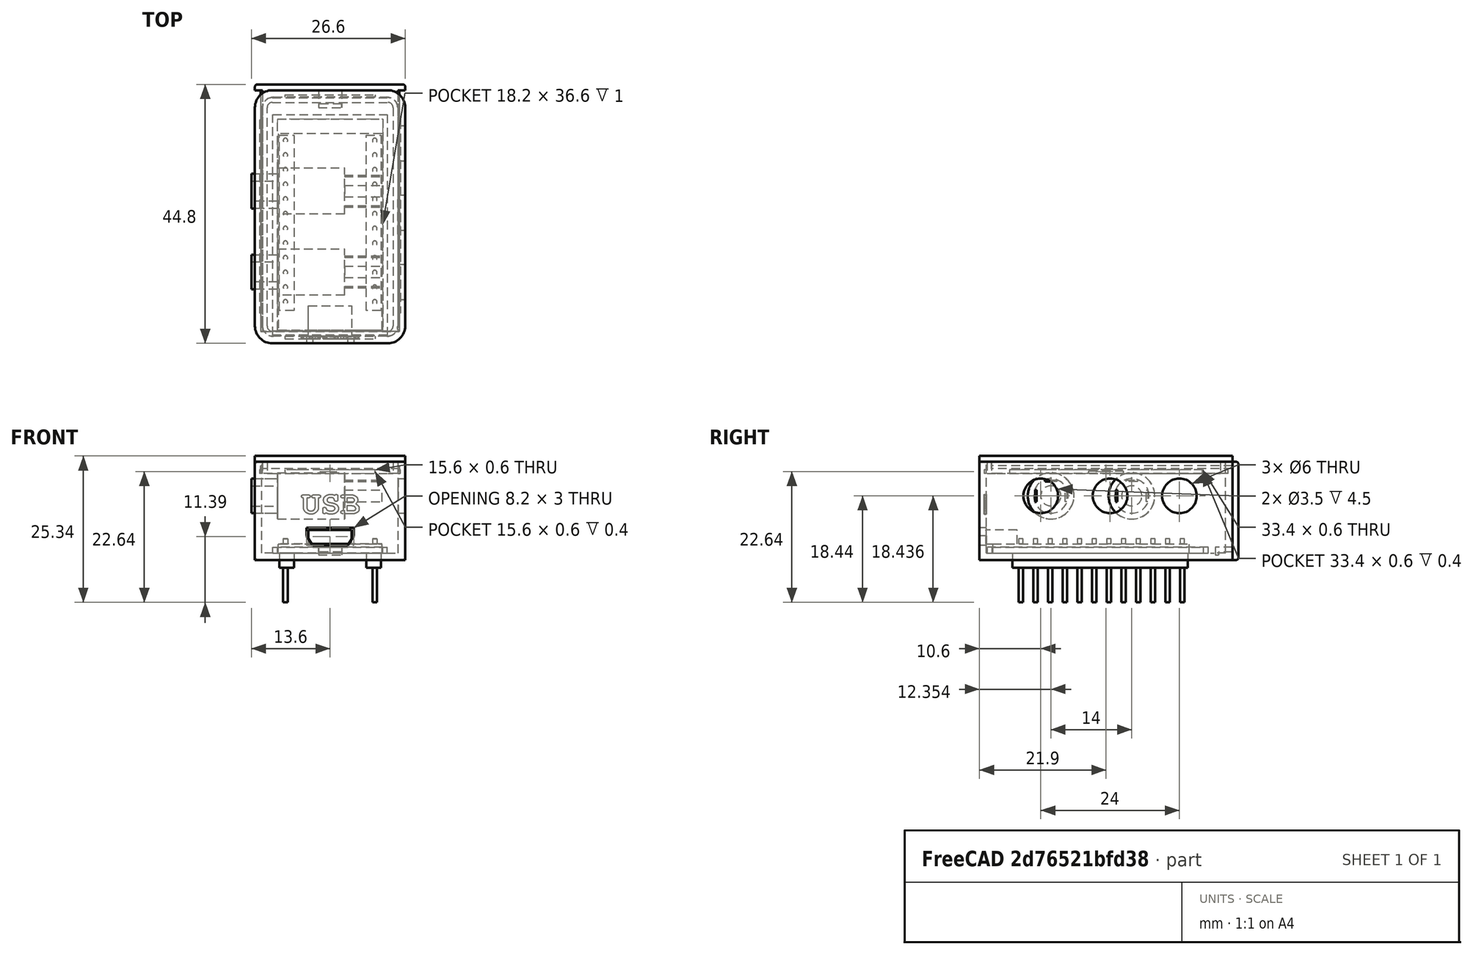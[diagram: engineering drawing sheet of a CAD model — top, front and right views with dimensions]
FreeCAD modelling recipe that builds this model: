
FCSTD DOCUMENT  (FreeCAD 0.18R4 (GitTag))
Label: FABI_mini
License: All rights reserved
LicenseURL: http://en.wikipedia.org/wiki/All_rights_reserved
objects: Sketcher::SketchObject×25, PartDesign::Pad×19, PartDesign::Body×6, PartDesign::Pocket×5, PartDesign::Fillet×4, Mesh::Feature×3, Part::Part2DObjectPython×2, Part::Extrusion×2, Part::Cut×2, PartDesign::Mirrored×1
note: 90 computed .brp shape members not serialized (recipe doc carries the construction recipe); baked Part::Feature solids carry a one-line shape summary decoded from their .brp

FEATURE [Sketcher::SketchObject] Sketch
  MapMode = 5
  Support = -> [XY_Plane]
  sketch-geometry (4):
    g0: LineSegment StartX=-13 StartY=24.5 StartZ=0 EndX=13 EndY=24.5 EndZ=0
    g1: LineSegment StartX=13 StartY=24.5 StartZ=0 EndX=13 EndY=-19.3 EndZ=0
    g2: LineSegment StartX=13 StartY=-19.3 StartZ=0 EndX=-13 EndY=-19.3 EndZ=0
    g3: LineSegment StartX=-13 StartY=-19.3 StartZ=0 EndX=-13 EndY=24.5 EndZ=0
  constraints (12):
    c: Coincident(g0,g1)
    c: Coincident(g1,g2)
    c: Coincident(g2,g3)
    c: Coincident(g3,g0)
    c: Horizontal(g0)
    c: Horizontal(g2)
    c: Vertical(g1)
    c: Vertical(g3)
    c: DistanceX(g0,g0) = 26
    c: DistanceY(g3,g3) = 43.8
    c: DistanceY(g2,g-1) = 19.3
    c: DistanceX(g2,g-1) = 13
FEATURE [PartDesign::Pad] Pad
  Length = 17
  Length2 = 100
  Profile = -> Sketch
  Refine = true
  Type = 0
FEATURE [Sketcher::SketchObject] CopyCopySketch002
  sketch-geometry (34):
    g0: Circle CenterX=32.8 CenterY=1.27 CenterZ=0 NormalX=0 NormalY=0 NormalZ=1 AngleXU=0 Radius=0.4
    g1: Circle CenterX=30.26 CenterY=1.27 CenterZ=0 NormalX=0 NormalY=0 NormalZ=1 AngleXU=0 Radius=0.4
    g2: Circle CenterX=27.72 CenterY=1.27 CenterZ=0 NormalX=0 NormalY=0 NormalZ=1 AngleXU=0 Radius=0.4
    g3: Circle CenterX=25.18 CenterY=1.27 CenterZ=0 NormalX=0 NormalY=0 NormalZ=1 AngleXU=0 Radius=0.4
    g4: Circle CenterX=22.64 CenterY=1.27 CenterZ=0 NormalX=0 NormalY=0 NormalZ=1 AngleXU=0 Radius=0.4
    g5: Circle CenterX=20.1 CenterY=1.27 CenterZ=0 NormalX=0 NormalY=0 NormalZ=1 AngleXU=0 Radius=0.4
    g6: Circle CenterX=17.56 CenterY=1.27 CenterZ=0 NormalX=0 NormalY=0 NormalZ=1 AngleXU=0 Radius=0.4
    g7: Circle CenterX=15.02 CenterY=1.27 CenterZ=0 NormalX=0 NormalY=0 NormalZ=1 AngleXU=0 Radius=0.4
    g8: Circle CenterX=12.48 CenterY=1.27 CenterZ=0 NormalX=0 NormalY=0 NormalZ=1 AngleXU=0 Radius=0.4
    g9: Circle CenterX=9.94 CenterY=1.27 CenterZ=0 NormalX=0 NormalY=0 NormalZ=1 AngleXU=0 Radius=0.4
    g10: Circle CenterX=7.4 CenterY=1.27 CenterZ=0 NormalX=0 NormalY=0 NormalZ=1 AngleXU=0 Radius=0.4
    g11: Circle CenterX=4.86 CenterY=1.27 CenterZ=0 NormalX=0 NormalY=0 NormalZ=1 AngleXU=0 Radius=0.4
    g12: LineSegment [constr] StartX=33.2 StartY=1.27 StartZ=0 EndX=3.66 EndY=1.27 EndZ=0
    g13: LineSegment [constr] StartX=34 StartY=0 StartZ=0 EndX=3.66 EndY=0 EndZ=0
    g14: LineSegment [constr] StartX=3.66 StartY=0 StartZ=0 EndX=3.66 EndY=2.54 EndZ=0
    g15: LineSegment [constr] StartX=3.66 StartY=2.54 StartZ=0 EndX=34 EndY=2.54 EndZ=0
    g16: LineSegment [constr] StartX=34 StartY=2.54 StartZ=0 EndX=34 EndY=0 EndZ=0
    g17: Circle CenterX=32.8 CenterY=16.73 CenterZ=0 NormalX=0 NormalY=0 NormalZ=1 AngleXU=0 Radius=0.4
    g18: Circle CenterX=30.26 CenterY=16.73 CenterZ=0 NormalX=0 NormalY=0 NormalZ=1 AngleXU=0 Radius=0.4
    g19: Circle CenterX=27.72 CenterY=16.73 CenterZ=0 NormalX=0 NormalY=0 NormalZ=1 AngleXU=0 Radius=0.4
    g20: Circle CenterX=25.18 CenterY=16.73 CenterZ=0 NormalX=0 NormalY=0 NormalZ=1 AngleXU=0 Radius=0.4
    g21: Circle CenterX=22.64 CenterY=16.73 CenterZ=0 NormalX=0 NormalY=0 NormalZ=1 AngleXU=0 Radius=0.4
    g22: Circle CenterX=20.1 CenterY=16.73 CenterZ=0 NormalX=0 NormalY=0 NormalZ=1 AngleXU=0 Radius=0.4
    g23: Circle CenterX=17.56 CenterY=16.73 CenterZ=0 NormalX=0 NormalY=0 NormalZ=1 AngleXU=0 Radius=0.4
    g24: Circle CenterX=15.02 CenterY=16.73 CenterZ=0 NormalX=0 NormalY=0 NormalZ=1 AngleXU=0 Radius=0.4
    g25: Circle CenterX=12.48 CenterY=16.73 CenterZ=0 NormalX=0 NormalY=0 NormalZ=1 AngleXU=0 Radius=0.4
    g26: Circle CenterX=9.94 CenterY=16.73 CenterZ=0 NormalX=0 NormalY=0 NormalZ=1 AngleXU=0 Radius=0.4
    g27: Circle CenterX=7.4 CenterY=16.73 CenterZ=0 NormalX=0 NormalY=0 NormalZ=1 AngleXU=0 Radius=0.4
    g28: Circle CenterX=4.86 CenterY=16.73 CenterZ=0 NormalX=0 NormalY=0 NormalZ=1 AngleXU=0 Radius=0.4
    g29: LineSegment [constr] StartX=33.2 StartY=16.73 StartZ=0 EndX=3.66 EndY=16.73 EndZ=0
    g30: LineSegment [constr] StartX=34 StartY=15.46 StartZ=0 EndX=3.66 EndY=15.46 EndZ=0
    g31: LineSegment [constr] StartX=3.66 StartY=15.46 StartZ=0 EndX=3.66 EndY=18 EndZ=0
    g32: LineSegment [constr] StartX=3.66 StartY=18 StartZ=0 EndX=34 EndY=18 EndZ=0
    g33: LineSegment [constr] StartX=34 StartY=18 StartZ=0 EndX=34 EndY=15.46 EndZ=0
  constraints (104):
    c: Radius(g0) = 0.4
    c: Equal(g0,g1) = 0.4
    c: Equal(g0,g2) = 0.4
    c: Equal(g2,g3) = 0.4
    c: Equal(g0,g4) = 0.4
    c: Equal(g4,g5) = 0.4
    c: Equal(g4,g6) = 0.4
    c: Equal(g6,g7) = 0.4
    c: Equal(g8,g9) = 0.4
    c: Equal(g8,g10) = 0.4
    c: Equal(g10,g11) = 0.4
    c: Horizontal(g12)
    c: PointOnObject(g11,g12)
    c: PointOnObject(g10,g12)
    c: PointOnObject(g9,g12)
    c: PointOnObject(g8,g12)
    c: PointOnObject(g7,g12)
    c: PointOnObject(g6,g12)
    c: PointOnObject(g5,g12)
    c: PointOnObject(g4,g12)
    c: PointOnObject(g3,g12)
    c: PointOnObject(g2,g12)
    c: PointOnObject(g1,g12)
    c: PointOnObject(g0,g12)
    c: DistanceX(g1,g0) = 2.54
    c: DistanceX(g2,g1) = 2.54
    c: DistanceX(g3,g2) = 2.54
    c: DistanceX(g4,g3) = 2.54
    c: DistanceX(g5,g4) = 2.54
    c: DistanceX(g6,g5) = 2.54
    c: DistanceX(g7,g6) = 2.54
    c: DistanceX(g8,g7) = 2.54
    c: DistanceX(g9,g8) = 2.54
    c: DistanceX(g10,g9) = 2.54
    c: DistanceX(g11,g10) = 2.54
    c: Coincident(g13,g14)
    c: Coincident(g14,g15)
    c: Coincident(g15,g16)
    c: Coincident(g16,g13)
    c: Horizontal(g13)
    c: Horizontal(g15)
    c: Vertical(g14)
    c: Vertical(g16)
    c: DistanceY(g14,g14) = 2.54
    c: DistanceY(g13,g0) = 1.27
    c: DistanceX(g12,g15) = 0.8
    c: PointOnObject(g12,g0)
    c: Equal(g7,g8)
    c: DistanceX(g14,g11) = 1.2
    c: Equal(g0,g17) = 0.4
    c: Equal(g17,g18) = 0.4
    c: Equal(g17,g19) = 0.4
    c: Equal(g19,g20) = 0.4
    c: Equal(g17,g21) = 0.4
    c: Equal(g21,g22) = 0.4
    c: Equal(g21,g23) = 0.4
    c: Equal(g23,g24) = 0.4
    c: Equal(g25,g26) = 0.4
    c: Equal(g25,g27) = 0.4
    c: Equal(g27,g28) = 0.4
    c: Horizontal(g29)
    c: PointOnObject(g28,g29)
    c: PointOnObject(g27,g29)
    c: PointOnObject(g26,g29)
    c: PointOnObject(g25,g29)
    c: PointOnObject(g24,g29)
    c: PointOnObject(g23,g29)
    c: PointOnObject(g22,g29)
    c: PointOnObject(g21,g29)
    c: PointOnObject(g20,g29)
    c: PointOnObject(g19,g29)
    c: PointOnObject(g18,g29)
    c: PointOnObject(g17,g29)
    c: DistanceX(g18,g17) = 2.54
    c: DistanceX(g19,g18) = 2.54
    c: DistanceX(g20,g19) = 2.54
    c: DistanceX(g21,g20) = 2.54
    c: DistanceX(g22,g21) = 2.54
    c: DistanceX(g23,g22) = 2.54
    c: DistanceX(g24,g23) = 2.54
    c: DistanceX(g25,g24) = 2.54
    c: DistanceX(g26,g25) = 2.54
    c: DistanceX(g27,g26) = 2.54
    c: DistanceX(g28,g27) = 2.54
    c: Coincident(g30,g31)
    c: Coincident(g31,g32)
    c: Coincident(g32,g33)
    c: Coincident(g33,g30)
    c: Horizontal(g30)
    c: Horizontal(g32)
    c: Vertical(g31)
    c: Vertical(g33)
    c: Equal(g14,g31) = 2.54
    c: DistanceY(g30,g17) = 1.27
    c: DistanceX(g29,g32) = 0.8
    c: PointOnObject(g29,g17)
    c: Equal(g24,g25)
    c: DistanceX(g31,g28) = 1.2
    c: PointOnObject(g12,g14)
    c: PointOnObject(g29,g31)
    c: DistanceY(g-1,g31) = 18
    c: DistanceX(g30,g14) = 0
    c: DistanceY(g13,g-1) = 0
    c: DistanceX(g-1,g13) = 3.66
FEATURE [Sketcher::SketchObject] Sketch001
  MapMode = 5
  Support = -> [XY_Plane001]
  sketch-geometry (4):
    g0: LineSegment StartX=0 StartY=0 StartZ=0 EndX=34 EndY=0 EndZ=0
    g1: LineSegment StartX=34 StartY=0 StartZ=0 EndX=34 EndY=18 EndZ=0
    g2: LineSegment StartX=34 StartY=18 StartZ=0 EndX=0 EndY=18 EndZ=0
    g3: LineSegment StartX=0 StartY=18 StartZ=0 EndX=0 EndY=0 EndZ=0
  constraints (11):
    c: Coincident(g2,g3)
    c: Coincident(g3,g0)
    c: Horizontal(g0)
    c: Horizontal(g2)
    c: Vertical(g1)
    c: Vertical(g3)
    c: Coincident(g0,g-1)
    c: DistanceY(g3,g3) = 18
    c: DistanceX(g2,g2) = 34
    c: Coincident(g1,g0)
    c: Coincident(g2,g1)
FEATURE [PartDesign::Pad] Pad001
  Length = 1.6
  Length2 = 100
  Profile = -> Sketch001
  Refine = true
  Type = 0
FEATURE [Sketcher::SketchObject] Sketch002
  MapMode = 5
  Support = -> [XY_Plane001]
  sketch-geometry (8):
    g0: LineSegment StartX=3.4 StartY=17.8 StartZ=0 EndX=33.74 EndY=17.8 EndZ=0
    g1: LineSegment StartX=33.74 StartY=17.8 StartZ=0 EndX=33.74 EndY=15.26 EndZ=0
    g2: LineSegment StartX=33.74 StartY=15.26 StartZ=0 EndX=3.4 EndY=15.26 EndZ=0
    g3: LineSegment StartX=3.4 StartY=15.26 StartZ=0 EndX=3.4 EndY=17.8 EndZ=0
    g4: LineSegment StartX=3.4 StartY=2.74 StartZ=0 EndX=33.74 EndY=2.74 EndZ=0
    g5: LineSegment StartX=33.74 StartY=2.74 StartZ=0 EndX=33.74 EndY=0.2 EndZ=0
    g6: LineSegment StartX=33.74 StartY=0.2 StartZ=0 EndX=3.4 EndY=0.2 EndZ=0
    g7: LineSegment StartX=3.4 StartY=0.2 StartZ=0 EndX=3.4 EndY=2.74 EndZ=0
  constraints (24):
    c: Coincident(g0,g1)
    c: Coincident(g1,g2)
    c: Coincident(g2,g3)
    c: Coincident(g3,g0)
    c: Horizontal(g0)
    c: Horizontal(g2)
    c: Vertical(g1)
    c: Vertical(g3)
    c: DistanceX(g0,g0) = 30.34
    c: DistanceY(g3,g3) = 2.54
    c: DistanceX(g-1,g2) = 3.4
    c: Coincident(g4,g5)
    c: Coincident(g5,g6)
    c: Coincident(g6,g7)
    c: Coincident(g7,g4)
    c: Horizontal(g4)
    c: Horizontal(g6)
    c: Vertical(g5)
    c: Vertical(g7)
    c: Equal(g0,g4) = 30.34
    c: Equal(g3,g7) = 2.54
    c: DistanceY(g-1,g6) = 0.2
    c: DistanceX(g2,g4) = 0
    c: DistanceY(g6,g0) = 17.6
FEATURE [PartDesign::Pad] Pad002  label="PinHeaderBody"
  BaseFeature = -> Pad001
  Length = 2.54
  Length2 = 100
  Profile = -> Sketch002
  Refine = true
  Reversed = true
  Type = 0
FEATURE [PartDesign::Pad] Pad003  label="PinHeaderPins"
  BaseFeature = -> Pad002
  Length = 2.5
  Length2 = 8.54
  Profile = -> CopyCopySketch002
  Refine = true
  Reversed = true
  Type = 4
FEATURE [Sketcher::SketchObject] Sketch003  label="microUsb"
  MapMode = 5
  Placement = pos=(0,0,1.6) rot=(0,0,1;0rad)
  Support = -> [Pad003]
  sketch-geometry (4):
    g0: LineSegment StartX=-1.2 StartY=12.75 StartZ=0 EndX=4.2 EndY=12.75 EndZ=0
    g1: LineSegment StartX=4.2 StartY=12.75 StartZ=0 EndX=4.2 EndY=5.25 EndZ=0
    g2: LineSegment StartX=4.2 StartY=5.25 StartZ=0 EndX=-1.2 EndY=5.25 EndZ=0
    g3: LineSegment StartX=-1.2 StartY=5.25 StartZ=0 EndX=-1.2 EndY=12.75 EndZ=0
  constraints (12):
    c: Coincident(g0,g1)
    c: Coincident(g1,g2)
    c: Coincident(g2,g3)
    c: Coincident(g3,g0)
    c: Horizontal(g0)
    c: Horizontal(g2)
    c: Vertical(g1)
    c: Vertical(g3)
    c: DistanceY(g3,g3) = 7.5
    c: DistanceX(g0,g0) = 5.4
    c: DistanceX(g2,g-1) = 1.2
    c: DistanceY(g-1,g2) = 5.25
FEATURE [PartDesign::Pad] Pad004  label="MicroUSB"
  BaseFeature = -> Pad003
  Length = 2.4
  Length2 = 100
  Profile = -> Sketch003
  Refine = true
  Type = 0
FEATURE [PartDesign::Body] Body001  label="ProMicro001"
  Group = -> [Sketch001,Pad001,Sketch002,Pad002,Pad003,Sketch003,Pad004]
  Origin = -> Origin001
  Placement = pos=(9,-17,1.2) rot=(0,0,1;1.5708rad)
  Tip = -> Pad004
FEATURE [Sketcher::SketchObject] Sketch004
  ExternalGeometry = -> [Sketch]
  MapMode = 5
  Placement = pos=(0,0,1.2) rot=(0,0,1;0rad)
  sketch-geometry (4):
    g0: LineSegment StartX=-11.8 StartY=23.3 StartZ=0 EndX=11.8 EndY=23.3 EndZ=0
    g1: LineSegment StartX=11.8 StartY=23.3 StartZ=0 EndX=11.8 EndY=-18.1 EndZ=0
    g2: LineSegment StartX=11.8 StartY=-18.1 StartZ=0 EndX=-11.8 EndY=-18.1 EndZ=0
    g3: LineSegment StartX=-11.8 StartY=-18.1 StartZ=0 EndX=-11.8 EndY=23.3 EndZ=0
  constraints (12):
    c: Coincident(g0,g1)
    c: Coincident(g1,g2)
    c: Coincident(g2,g3)
    c: Horizontal(g0)
    c: Horizontal(g2)
    c: Vertical(g1)
    c: Vertical(g3)
    c: Coincident(g0,g3)
    c: DistanceY(g-3,g2) = 1.2
    c: DistanceY(g-4,g0) = -1.2
    c: DistanceX(g1,g-4) = 1.2
    c: DistanceX(g-3,g2) = 1.2
FEATURE [PartDesign::Pocket] Pocket
  BaseFeature = -> Pad
  Length = 31
  Length2 = 100
  Profile = -> Sketch004
  Refine = true
  Reversed = true
  Type = 1
FEATURE [Sketcher::SketchObject] Sketch006  label="ProMicro"
  MapMode = 5
  Placement = pos=(0,-18.1,0) rot=(0,0.707107,0.707107;3.14159rad)
  Support = -> [Pocket]
  sketch-geometry (6):
    g0: LineSegment StartX=-4.1 StartY=5.55 StartZ=0 EndX=4.1 EndY=5.55 EndZ=0
    g1: LineSegment StartX=4.1 StartY=5.55 StartZ=0 EndX=4.1 EndY=4.15 EndZ=0
    g2: LineSegment StartX=-4.1 StartY=4.15 StartZ=0 EndX=-4.1 EndY=5.55 EndZ=0
    g3: LineSegment StartX=-3 StartY=2.55 StartZ=0 EndX=3 EndY=2.55 EndZ=0
    g4: LineSegment StartX=3 StartY=2.55 StartZ=0 EndX=4.1 EndY=4.15 EndZ=0
    g5: LineSegment StartX=-4.1 StartY=4.15 StartZ=0 EndX=-3 EndY=2.55 EndZ=0
  constraints (18):
    c: Coincident(g0,g1)
    c: Coincident(g2,g0)
    c: Horizontal(g0)
    c: Vertical(g1)
    c: Vertical(g2)
    c: DistanceX(g0,g0) = 8.2
    c: Horizontal(g3)
    c: DistanceY(g3,g0) = 3
    c: DistanceY(g1,g1) = 1.4
    c: Coincident(g4,g3)
    c: Coincident(g4,g1)
    c: Equal(g2,g1)
    c: Coincident(g5,g2)
    c: Coincident(g5,g3)
    c: Equal(g5,g4)
    c: DistanceX(g3,g3) = 6
    c: DistanceX(g3,g-1) = 3
    c: DistanceY(g-1,g3) = 2.55
FEATURE [PartDesign::Pocket] Pocket001  label="ProMicroCut"
  BaseFeature = -> Pocket
  Length = 5
  Length2 = 100
  Profile = -> Sketch006
  Refine = true
  Type = 2
FEATURE [Sketcher::SketchObject] Sketch007
  MapMode = 5
  Placement = pos=(0,0,0) rot=(0.57735,0.57735,0.57735;2.0944rad)
  Support = -> [YZ_Plane002]
  sketch-geometry (1):
    g0: Circle CenterX=-5.05387 CenterY=6.09633 CenterZ=0 NormalX=0 NormalY=0 NormalZ=1 AngleXU=0 Radius=4
  constraints (1):
    c: Radius(g0) = 4
FEATURE [PartDesign::Pad] Pad005
  Length = 11.6
  Length2 = 100
  Placement = pos=(0,0,0) rot=(0.57735,0.57735,0.57735;2.0944rad)
  Profile = -> Sketch007
  Refine = true
  Type = 0
FEATURE [Sketcher::SketchObject] Sketch008
  ExternalGeometry = -> [Pad005]
  MapMode = 5
  Placement = pos=(11.6,-2.6e-15,2.6e-15) rot=(0.57735,0.57735,0.57735;2.0944rad)
  Support = -> [Pad005]
  sketch-geometry (2):
    g0: Circle CenterX=-5.05387 CenterY=6.09633 CenterZ=0 NormalX=0 NormalY=0 NormalZ=1 AngleXU=0 Radius=3
    g1: Circle CenterX=-5.05387 CenterY=6.09633 CenterZ=0 NormalX=0 NormalY=0 NormalZ=1 AngleXU=0 Radius=1.75
  constraints (4):
    c: Radius(g0) = 3
    c: Coincident(g0,g-3)
    c: Coincident(g1,g0)
    c: Radius(g1) = 1.75
FEATURE [PartDesign::Pad] Pad006
  BaseFeature = -> Pad005
  Length = 4.5
  Length2 = 100
  Placement = pos=(0,0,0) rot=(0.57735,0.57735,0.57735;2.0944rad)
  Profile = -> Sketch008
  Refine = true
  Type = 0
FEATURE [Sketcher::SketchObject] Sketch009
  ExternalGeometry = -> [Pad006]
  MapMode = 5
  Placement = pos=(0,0,0) rot=(0.57735,0.57735,-0.57735;4.18879rad)
  Support = -> [Pad006]
  sketch-geometry (12):
    g0: LineSegment StartX=-6.05387 StartY=-8.59633 StartZ=0 EndX=-4.05387 EndY=-8.59633 EndZ=0
    g1: LineSegment StartX=-4.05387 StartY=-8.59633 StartZ=0 EndX=-4.05387 EndY=-8.84633 EndZ=0
    g2: LineSegment StartX=-4.05387 StartY=-8.84633 StartZ=0 EndX=-6.05387 EndY=-8.84633 EndZ=0
    g3: LineSegment StartX=-6.05387 StartY=-8.84633 StartZ=0 EndX=-6.05387 EndY=-8.59633 EndZ=0
    g4: LineSegment StartX=-7.80387 StartY=-5.09633 StartZ=0 EndX=-7.55387 EndY=-5.09633 EndZ=0
    g5: LineSegment StartX=-7.55387 StartY=-5.09633 StartZ=0 EndX=-7.55387 EndY=-7.09633 EndZ=0
    g6: LineSegment StartX=-7.55387 StartY=-7.09633 StartZ=0 EndX=-7.80387 EndY=-7.09633 EndZ=0
    g7: LineSegment StartX=-7.80387 StartY=-7.09633 StartZ=0 EndX=-7.80387 EndY=-5.09633 EndZ=0
    g8: LineSegment StartX=-2.55387 StartY=-5.09633 StartZ=0 EndX=-2.30387 EndY=-5.09633 EndZ=0
    g9: LineSegment StartX=-2.30387 StartY=-5.09633 StartZ=0 EndX=-2.30387 EndY=-7.09633 EndZ=0
    g10: LineSegment StartX=-2.30387 StartY=-7.09633 StartZ=0 EndX=-2.55387 EndY=-7.09633 EndZ=0
    g11: LineSegment StartX=-2.55387 StartY=-7.09633 StartZ=0 EndX=-2.55387 EndY=-5.09633 EndZ=0
  constraints (36):
    c: Coincident(g0,g1)
    c: Coincident(g1,g2)
    c: Coincident(g2,g3)
    c: Coincident(g3,g0)
    c: Horizontal(g0)
    c: Horizontal(g2)
    c: Vertical(g1)
    c: Vertical(g3)
    c: DistanceY(g1,g1) = 0.25
    c: DistanceX(g0,g0) = 2
    c: Coincident(g4,g5)
    c: Coincident(g5,g6)
    c: Coincident(g6,g7)
    c: Coincident(g7,g4)
    c: Horizontal(g4)
    c: Horizontal(g6)
    c: Vertical(g5)
    c: Vertical(g7)
    c: Coincident(g8,g9)
    c: Coincident(g9,g10)
    c: Coincident(g10,g11)
    c: Coincident(g11,g8)
    c: Horizontal(g8)
    c: Horizontal(g10)
    c: Vertical(g9)
    c: Vertical(g11)
    c: DistanceY(g7,g7) = 2
    c: DistanceY(g11,g11) = 2
    c: DistanceX(g4,g4) = 0.25
    c: DistanceX(g8,g8) = 0.25
    c: DistanceX(g5,g-3) = 2.5
    c: DistanceX(g-3,g8) = 2.5
    c: DistanceY(g5,g-3) = 1
    c: DistanceY(g10,g-3) = 1
    c: DistanceY(g0,g-3) = 2.5
    c: DistanceX(g0,g-3) = 1
FEATURE [PartDesign::Pad] Pad007
  BaseFeature = -> Pad006
  Length = 6.5
  Length2 = 100
  Placement = pos=(0,0,0) rot=(0.57735,0.57735,0.57735;2.0944rad)
  Profile = -> Sketch009
  Refine = true
  Type = 0
FEATURE [PartDesign::Body] Body002  label="JackPlug"
  Group = -> [Sketch007,Pad005,Sketch008,Pad006,Sketch009,Pad007]
  Origin = -> Origin002
  Placement = pos=(2.5,-12,5) rot=(0,0,1;3.14159rad)
  Tip = -> Pad007
FEATURE [Sketcher::SketchObject] Sketch010
  MapMode = 5
  Placement = pos=(0,0,0) rot=(0.57735,0.57735,0.57735;2.0944rad)
  Support = -> [YZ_Plane003]
  sketch-geometry (1):
    g0: Circle CenterX=-5.05387 CenterY=6.09633 CenterZ=0 NormalX=0 NormalY=0 NormalZ=1 AngleXU=0 Radius=4
  constraints (1):
    c: Radius(g0) = 4
FEATURE [PartDesign::Pad] Pad009
  Length = 11.6
  Length2 = 100
  Placement = pos=(0,0,0) rot=(0.57735,0.57735,0.57735;2.0944rad)
  Profile = -> Sketch010
  Refine = true
  Type = 0
FEATURE [Sketcher::SketchObject] Sketch012
  ExternalGeometry = -> [Pad009]
  MapMode = 5
  Placement = pos=(11.6,-2.6e-15,2.6e-15) rot=(0.57735,0.57735,0.57735;2.0944rad)
  Support = -> [Pad009]
  sketch-geometry (2):
    g0: Circle CenterX=-5.05387 CenterY=6.09633 CenterZ=0 NormalX=0 NormalY=0 NormalZ=1 AngleXU=0 Radius=3
    g1: Circle CenterX=-5.05387 CenterY=6.09633 CenterZ=0 NormalX=0 NormalY=0 NormalZ=1 AngleXU=0 Radius=1.75
  constraints (4):
    c: Radius(g0) = 3
    c: Coincident(g0,g-3)
    c: Coincident(g1,g0)
    c: Radius(g1) = 1.75
FEATURE [PartDesign::Pad] Pad008
  BaseFeature = -> Pad009
  Length = 4.5
  Length2 = 100
  Placement = pos=(0,0,0) rot=(0.57735,0.57735,0.57735;2.0944rad)
  Profile = -> Sketch012
  Refine = true
  Type = 0
FEATURE [Sketcher::SketchObject] Sketch011
  ExternalGeometry = -> [Pad008]
  MapMode = 5
  Placement = pos=(0,0,0) rot=(0.57735,0.57735,-0.57735;4.18879rad)
  Support = -> [Pad008]
  sketch-geometry (12):
    g0: LineSegment StartX=-6.05387 StartY=-8.59633 StartZ=0 EndX=-4.05387 EndY=-8.59633 EndZ=0
    g1: LineSegment StartX=-4.05387 StartY=-8.59633 StartZ=0 EndX=-4.05387 EndY=-8.84633 EndZ=0
    g2: LineSegment StartX=-4.05387 StartY=-8.84633 StartZ=0 EndX=-6.05387 EndY=-8.84633 EndZ=0
    g3: LineSegment StartX=-6.05387 StartY=-8.84633 StartZ=0 EndX=-6.05387 EndY=-8.59633 EndZ=0
    g4: LineSegment StartX=-7.80387 StartY=-5.09633 StartZ=0 EndX=-7.55387 EndY=-5.09633 EndZ=0
    g5: LineSegment StartX=-7.55387 StartY=-5.09633 StartZ=0 EndX=-7.55387 EndY=-7.09633 EndZ=0
    g6: LineSegment StartX=-7.55387 StartY=-7.09633 StartZ=0 EndX=-7.80387 EndY=-7.09633 EndZ=0
    g7: LineSegment StartX=-7.80387 StartY=-7.09633 StartZ=0 EndX=-7.80387 EndY=-5.09633 EndZ=0
    g8: LineSegment StartX=-2.55387 StartY=-5.09633 StartZ=0 EndX=-2.30387 EndY=-5.09633 EndZ=0
    g9: LineSegment StartX=-2.30387 StartY=-5.09633 StartZ=0 EndX=-2.30387 EndY=-7.09633 EndZ=0
    g10: LineSegment StartX=-2.30387 StartY=-7.09633 StartZ=0 EndX=-2.55387 EndY=-7.09633 EndZ=0
    g11: LineSegment StartX=-2.55387 StartY=-7.09633 StartZ=0 EndX=-2.55387 EndY=-5.09633 EndZ=0
  constraints (36):
    c: Coincident(g0,g1)
    c: Coincident(g1,g2)
    c: Coincident(g2,g3)
    c: Coincident(g3,g0)
    c: Horizontal(g0)
    c: Horizontal(g2)
    c: Vertical(g1)
    c: Vertical(g3)
    c: DistanceY(g1,g1) = 0.25
    c: DistanceX(g0,g0) = 2
    c: Coincident(g4,g5)
    c: Coincident(g5,g6)
    c: Coincident(g6,g7)
    c: Coincident(g7,g4)
    c: Horizontal(g4)
    c: Horizontal(g6)
    c: Vertical(g5)
    c: Vertical(g7)
    c: Coincident(g8,g9)
    c: Coincident(g9,g10)
    c: Coincident(g10,g11)
    c: Coincident(g11,g8)
    c: Horizontal(g8)
    c: Horizontal(g10)
    c: Vertical(g9)
    c: Vertical(g11)
    c: DistanceY(g7,g7) = 2
    c: DistanceY(g11,g11) = 2
    c: DistanceX(g4,g4) = 0.25
    c: DistanceX(g8,g8) = 0.25
    c: DistanceX(g5,g-3) = 2.5
    c: DistanceX(g-3,g8) = 2.5
    c: DistanceY(g5,g-3) = 1
    c: DistanceY(g10,g-3) = 1
    c: DistanceY(g0,g-3) = 2.5
    c: DistanceX(g0,g-3) = 1
FEATURE [PartDesign::Pad] Pad010
  BaseFeature = -> Pad008
  Length = 6.5
  Length2 = 100
  Placement = pos=(0,0,0) rot=(0.57735,0.57735,0.57735;2.0944rad)
  Profile = -> Sketch011
  Refine = true
  Type = 0
FEATURE [PartDesign::Body] Body003  label="JackPlug001"
  Group = -> [Sketch010,Pad009,Sketch012,Pad008,Sketch011,Pad010]
  Origin = -> Origin003
  Placement = pos=(2.5,2,5) rot=(0,0,1;3.14159rad)
  Tip = -> Pad010
FEATURE [Sketcher::SketchObject] Sketch013
  MapMode = 5
  Placement = pos=(13,0,0) rot=(0.57735,0.57735,0.57735;2.0944rad)
  Support = -> [Pocket001]
  sketch-geometry (3):
    g0: Circle CenterX=-8.7 CenterY=11.1 CenterZ=0 NormalX=0 NormalY=0 NormalZ=1 AngleXU=0 Radius=3
    g1: Circle CenterX=3.3 CenterY=11.1 CenterZ=0 NormalX=0 NormalY=0 NormalZ=1 AngleXU=0 Radius=3
    g2: Circle CenterX=15.3 CenterY=11.1 CenterZ=0 NormalX=0 NormalY=0 NormalZ=1 AngleXU=0 Radius=3
  constraints (9):
    c: Radius(g0) = 3
    c: DistanceY(g-1,g0) = 11.1
    c: DistanceX(g0,g-1) = 8.7
    c: Equal(g0,g1) = 3.2
    c: Horizontal(g0,g1)
    c: DistanceX(g0,g1) = 12
    c: Horizontal(g2,g1)
    c: DistanceX(g1,g2) = 12
    c: Equal(g2,g1)
FEATURE [PartDesign::Pocket] Pocket002
  BaseFeature = -> Pocket001
  Length = 5
  Length2 = 100
  Offset = 5
  Profile = -> Sketch013
  Refine = true
  Type = 0
FEATURE [Sketcher::SketchObject] Sketch015
  MapMode = 5
  Placement = pos=(0,25.5,0) rot=(1,0,0;1.5708rad)
  sketch-geometry (4):
    g0: LineSegment StartX=-13 StartY=17 StartZ=0 EndX=13 EndY=17 EndZ=0
    g1: LineSegment StartX=13 StartY=17 StartZ=0 EndX=13 EndY=0 EndZ=0
    g2: LineSegment StartX=13 StartY=0 StartZ=0 EndX=-13 EndY=0 EndZ=0
    g3: LineSegment StartX=-13 StartY=0 StartZ=0 EndX=-13 EndY=17 EndZ=0
  constraints (11):
    c: Coincident(g0,g1)
    c: Coincident(g1,g2)
    c: Coincident(g2,g3)
    c: Coincident(g3,g0)
    c: Horizontal(g0)
    c: Horizontal(g2)
    c: Vertical(g1)
    c: Vertical(g3)
    c: Symmetric(g2,g1,g-1)
    c: DistanceX(g2,g1) = 26
    c: DistanceY(g3,g3) = 17
FEATURE [PartDesign::Pad] Pad011
  Length = 1
  Length2 = 100
  Placement = pos=(0,25.5,0) rot=(1,0,0;1.5708rad)
  Profile = -> Sketch015
  Refine = true
  Reversed = true
  Type = 0
FEATURE [Sketcher::SketchObject] Sketch016
  ExternalGeometry = -> [Pad011]
  MapMode = 5
  Placement = pos=(0,25.5,0) rot=(1,0,0;1.5708rad)
  Support = -> [Pad011]
  sketch-geometry (11):
    g0: LineSegment [constr] StartX=-12 StartY=16.3 StartZ=0 EndX=12 EndY=16.3 EndZ=0
    g1: LineSegment StartX=12 StartY=16.3 StartZ=0 EndX=12 EndY=15.8 EndZ=0
    g2: LineSegment StartX=12 StartY=15.8 StartZ=0 EndX=-12 EndY=15.8 EndZ=0
    g3: LineSegment StartX=-12 StartY=15.8 StartZ=0 EndX=-12 EndY=16.3 EndZ=0
    g4: LineSegment [constr] StartX=-12 StartY=15.8 StartZ=0 EndX=0 EndY=1.8e-15 EndZ=0
    g5: LineSegment [constr] StartX=12 StartY=15.8 StartZ=0 EndX=0 EndY=1.8e-15 EndZ=0
    g6: LineSegment StartX=-11.7 StartY=16.3 StartZ=0 EndX=-11.7 EndY=17 EndZ=0
    g7: LineSegment StartX=-11.7 StartY=17 StartZ=0 EndX=11.7 EndY=17 EndZ=0
    g8: LineSegment StartX=11.7 StartY=17 StartZ=0 EndX=11.7 EndY=16.3 EndZ=0
    g9: LineSegment StartX=-12 StartY=16.3 StartZ=0 EndX=-11.7 EndY=16.3 EndZ=0
    g10: LineSegment StartX=11.7 StartY=16.3 StartZ=0 EndX=12 EndY=16.3 EndZ=0
  constraints (30):
    c: Coincident(g0,g1)
    c: Coincident(g1,g2)
    c: Coincident(g2,g3)
    c: Coincident(g3,g0)
    c: Horizontal(g0)
    c: Horizontal(g2)
    c: Vertical(g1)
    c: Vertical(g3)
    c: DistanceY(g1,g1) = 0.5
    c: DistanceY(g0,g-4) = 0.7
    c: DistanceX(g0,g0) = 24
    c: Coincident(g4,g2)
    c: Coincident(g4,g-1)
    c: Coincident(g5,g1)
    c: Coincident(g5,g4)
    c: Equal(g4,g5)
    c: PointOnObject(g6,g0)
    c: Vertical(g6)
    c: Coincident(g6,g7)
    c: Horizontal(g7)
    c: Coincident(g7,g8)
    c: PointOnObject(g8,g0)
    c: Vertical(g8)
    c: Coincident(g9,g3)
    c: Coincident(g9,g6)
    c: Coincident(g10,g8)
    c: Coincident(g10,g1)
    c: Equal(g10,g9)
    c: DistanceX(g7,g7) = 23.4
    c: DistanceY(g6,g6) = 0.7
FEATURE [PartDesign::Pad] Pad012
  BaseFeature = -> Pad011
  Length = 41.75
  Length2 = 100
  Placement = pos=(0,25.5,0) rot=(1,0,0;1.5708rad)
  Profile = -> Sketch016
  Refine = true
  Type = 0
FEATURE [Sketcher::SketchObject] Sketch017
  MapMode = 5
  Placement = pos=(0,25.5,0) rot=(1,0,0;1.5708rad)
  Support = -> [Pad012]
  sketch-geometry (6):
    g0: LineSegment StartX=-2 StartY=2.2 StartZ=0 EndX=2 EndY=2.2 EndZ=0
    g1: LineSegment StartX=2 StartY=2.2 StartZ=0 EndX=2 EndY=1.4 EndZ=0
    g2: LineSegment StartX=2 StartY=1.4 StartZ=0 EndX=-2 EndY=1.4 EndZ=0
    g3: LineSegment StartX=-2 StartY=1.4 StartZ=0 EndX=-2 EndY=2.2 EndZ=0
    g4: LineSegment [constr] StartX=-2 StartY=1.4 StartZ=0 EndX=0 EndY=0 EndZ=0
    g5: LineSegment [constr] StartX=0 StartY=0 StartZ=0 EndX=2 EndY=1.4 EndZ=0
  constraints (16):
    c: Coincident(g0,g1)
    c: Coincident(g1,g2)
    c: Coincident(g2,g3)
    c: Coincident(g3,g0)
    c: Horizontal(g0)
    c: Horizontal(g2)
    c: Vertical(g1)
    c: Vertical(g3)
    c: Coincident(g4,g2)
    c: Coincident(g4,g-1)
    c: Coincident(g5,g-1)
    c: Coincident(g5,g1)
    c: Equal(g4,g5)
    c: DistanceY(g3,g3) = 0.8
    c: DistanceX(g0,g0) = 4
    c: DistanceY(g-1,g2) = 1.4
FEATURE [PartDesign::Pad] Pad013
  BaseFeature = -> Pad012
  Length = 3
  Length2 = 100
  Placement = pos=(0,25.5,0) rot=(1,0,0;1.5708rad)
  Profile = -> Sketch017
  Refine = true
  Type = 0
FEATURE [Sketcher::SketchObject] Sketch018
  ExternalGeometry = -> [Pad013]
  MapMode = 5
  Placement = pos=(0,25.5,1.4) rot=(1,0,0;3.14159rad)
  Support = -> [Pad013]
  sketch-geometry (4):
    g0: LineSegment StartX=-2 StartY=3 StartZ=0 EndX=2 EndY=3 EndZ=0
    g1: LineSegment StartX=2 StartY=3 StartZ=0 EndX=2 EndY=2.4 EndZ=0
    g2: LineSegment StartX=2 StartY=2.4 StartZ=0 EndX=-2 EndY=2.4 EndZ=0
    g3: LineSegment StartX=-2 StartY=2.4 StartZ=0 EndX=-2 EndY=3 EndZ=0
  constraints (10):
    c: Coincident(g0,g1)
    c: Coincident(g1,g2)
    c: Coincident(g2,g3)
    c: Coincident(g3,g0)
    c: Horizontal(g2)
    c: Vertical(g1)
    c: Vertical(g3)
    c: DistanceY(g3,g3) = 0.6
    c: Tangent(g0,g-3) = 1.5708
    c: Coincident(g0,g-3)
FEATURE [PartDesign::Pad] Pad014
  BaseFeature = -> Pad013
  Length = 0.5
  Length2 = 100
  Placement = pos=(0,25.5,0) rot=(1,0,0;1.5708rad)
  Profile = -> Sketch018
  Refine = true
  Type = 0
FEATURE [PartDesign::Fillet] Fillet001
  Base = -> Pad014 [Edge1,Edge2,Edge5,Edge13]
  BaseFeature = -> Pad014
  Placement = pos=(0,25.5,0) rot=(1,0,0;1.5708rad)
  Radius = 0.6
FEATURE [PartDesign::Fillet] Fillet002
  Base = -> Fillet001 [Face5]
  BaseFeature = -> Fillet001
  Placement = pos=(0,25.5,0) rot=(1,0,0;1.5708rad)
  Radius = 0.4
FEATURE [PartDesign::Body] Body004  label="Deckel"
  Group = -> [Sketch015,Pad011,Sketch016,Pad012,Sketch017,Pad013,Sketch018,Pad014,Fillet001,Fillet002]
  Origin = -> Origin004
  Placement = pos=(0,-1,0) rot=(0,0,1;0rad)
  Tip = -> Fillet002
FEATURE [Part::Part2DObjectPython] ShapeString002  # Draft 2D object (typed FeaturePython)
  FontFile = <path>
  MapMode = 5
  Placement = pos=(-5,-18.5,9) rot=(1,0,0;1.5708rad)
  Size = 2
  String = USB
  Tracking = 0
FEATURE [Part::Extrusion] Extrude
  Base = -> ShapeString002
  Dir = (0,-1,0)
  DirMode = 2
  FaceMakerClass = Part::FaceMakerBullseye
  LengthFwd = -0.4
  LengthRev = 0
  Placement = pos=(0,0,-1) rot=(0,0,1;0rad)
  Solid = false
  Symmetric = false
FEATURE [Part::Part2DObjectPython] ShapeString001  # Draft 2D object (typed FeaturePython)
  AttachmentOffset = pos=(-10,2,0) rot=(0,0,1;0rad)
  FontFile = <path>
  MapMode = 5
  Placement = pos=(11,-10.8,2) rot=(0.57735,0.57735,0.57735;2.0944rad)
  Size = 2.5
  String = 1 2 3
  Tracking = 1.8
FEATURE [Part::Extrusion] Extrude001
  Base = -> ShapeString001
  Dir = (1,-1e-16,2e-16)
  DirMode = 2
  FaceMakerClass = Part::FaceMakerBullseye
  LengthFwd = -0.4
  LengthRev = 0
  Solid = false
  Symmetric = false
FEATURE [Mesh::Feature] Mesh  label="Cut001 (Meshed)"
FEATURE [Sketcher::SketchObject] Sketch032  label="Logo"
  AttachmentOffset = pos=(0,0,0) rot=(0,0,1;1.5708rad)
  MapMode = 5
  Placement = pos=(0,25.5,17) rot=(0,0,1;4.71239rad)
  Support = -> [Fillet002]
  sketch-geometry (282):
    g0: BSplineCurve PolesCount=4 KnotsCount=2 Degree=3 IsPeriodic=0
    g1: BSplineCurve PolesCount=4 KnotsCount=2 Degree=3 IsPeriodic=0
    g2: BSplineCurve PolesCount=4 KnotsCount=2 Degree=3 IsPeriodic=0
    g3: BSplineCurve PolesCount=4 KnotsCount=2 Degree=3 IsPeriodic=0
    g4: BSplineCurve PolesCount=4 KnotsCount=2 Degree=3 IsPeriodic=0
    g5: BSplineCurve PolesCount=4 KnotsCount=2 Degree=3 IsPeriodic=0
    g6: BSplineCurve PolesCount=4 KnotsCount=2 Degree=3 IsPeriodic=0
    g7: BSplineCurve PolesCount=4 KnotsCount=2 Degree=3 IsPeriodic=0
    g8: BSplineCurve PolesCount=4 KnotsCount=2 Degree=3 IsPeriodic=0
    g9: BSplineCurve PolesCount=4 KnotsCount=2 Degree=3 IsPeriodic=0
    g10: BSplineCurve PolesCount=4 KnotsCount=2 Degree=3 IsPeriodic=0
    g11: BSplineCurve PolesCount=4 KnotsCount=2 Degree=3 IsPeriodic=0
    g12: BSplineCurve PolesCount=4 KnotsCount=2 Degree=3 IsPeriodic=0
    g13: BSplineCurve PolesCount=4 KnotsCount=2 Degree=3 IsPeriodic=0
    g14: BSplineCurve PolesCount=4 KnotsCount=2 Degree=3 IsPeriodic=0
    g15: BSplineCurve PolesCount=4 KnotsCount=2 Degree=3 IsPeriodic=0
    g16: BSplineCurve PolesCount=4 KnotsCount=2 Degree=3 IsPeriodic=0
    g17: BSplineCurve PolesCount=4 KnotsCount=2 Degree=3 IsPeriodic=0
    g18: BSplineCurve PolesCount=4 KnotsCount=2 Degree=3 IsPeriodic=0
    g19: BSplineCurve PolesCount=4 KnotsCount=2 Degree=3 IsPeriodic=0
    g20: BSplineCurve PolesCount=4 KnotsCount=2 Degree=3 IsPeriodic=0
    g21: BSplineCurve PolesCount=4 KnotsCount=2 Degree=3 IsPeriodic=0
    g22: BSplineCurve PolesCount=4 KnotsCount=2 Degree=3 IsPeriodic=0
    g23: BSplineCurve PolesCount=4 KnotsCount=2 Degree=3 IsPeriodic=0
    g24: BSplineCurve PolesCount=4 KnotsCount=2 Degree=3 IsPeriodic=0
    g25: BSplineCurve PolesCount=4 KnotsCount=2 Degree=3 IsPeriodic=0
    g26: BSplineCurve PolesCount=4 KnotsCount=2 Degree=3 IsPeriodic=0
    g27: BSplineCurve PolesCount=4 KnotsCount=2 Degree=3 IsPeriodic=0
    g28: BSplineCurve PolesCount=4 KnotsCount=2 Degree=3 IsPeriodic=0
    g29: BSplineCurve PolesCount=4 KnotsCount=2 Degree=3 IsPeriodic=0
    g30: BSplineCurve PolesCount=4 KnotsCount=2 Degree=3 IsPeriodic=0
    g31: BSplineCurve PolesCount=4 KnotsCount=2 Degree=3 IsPeriodic=0
    g32: BSplineCurve PolesCount=4 KnotsCount=2 Degree=3 IsPeriodic=0
    g33: BSplineCurve PolesCount=4 KnotsCount=2 Degree=3 IsPeriodic=0
    g34: BSplineCurve PolesCount=4 KnotsCount=2 Degree=3 IsPeriodic=0
    g35: BSplineCurve PolesCount=4 KnotsCount=2 Degree=3 IsPeriodic=0
    g36: BSplineCurve PolesCount=4 KnotsCount=2 Degree=3 IsPeriodic=0
    g37: BSplineCurve PolesCount=4 KnotsCount=2 Degree=3 IsPeriodic=0
    g38: BSplineCurve PolesCount=4 KnotsCount=2 Degree=3 IsPeriodic=0
    g39: BSplineCurve PolesCount=4 KnotsCount=2 Degree=3 IsPeriodic=0
    g40: BSplineCurve PolesCount=4 KnotsCount=2 Degree=3 IsPeriodic=0
    g41: BSplineCurve PolesCount=4 KnotsCount=2 Degree=3 IsPeriodic=0
    g42: BSplineCurve PolesCount=4 KnotsCount=2 Degree=3 IsPeriodic=0
    g43: BSplineCurve PolesCount=4 KnotsCount=2 Degree=3 IsPeriodic=0
    g44: BSplineCurve PolesCount=4 KnotsCount=2 Degree=3 IsPeriodic=0
    g45: BSplineCurve PolesCount=4 KnotsCount=2 Degree=3 IsPeriodic=0
    g46: BSplineCurve PolesCount=4 KnotsCount=2 Degree=3 IsPeriodic=0
    g47: BSplineCurve PolesCount=4 KnotsCount=2 Degree=3 IsPeriodic=0
    g48: BSplineCurve PolesCount=4 KnotsCount=2 Degree=3 IsPeriodic=0
    g49: BSplineCurve PolesCount=4 KnotsCount=2 Degree=3 IsPeriodic=0
    g50: BSplineCurve PolesCount=4 KnotsCount=2 Degree=3 IsPeriodic=0
    g51: BSplineCurve PolesCount=4 KnotsCount=2 Degree=3 IsPeriodic=0
    g52: BSplineCurve PolesCount=4 KnotsCount=2 Degree=3 IsPeriodic=0
    g53: BSplineCurve PolesCount=4 KnotsCount=2 Degree=3 IsPeriodic=0
    g54: BSplineCurve PolesCount=4 KnotsCount=2 Degree=3 IsPeriodic=0
    g55: BSplineCurve PolesCount=4 KnotsCount=2 Degree=3 IsPeriodic=0
    g56: BSplineCurve PolesCount=4 KnotsCount=2 Degree=3 IsPeriodic=0
    g57: BSplineCurve PolesCount=4 KnotsCount=2 Degree=3 IsPeriodic=0
    g58: BSplineCurve PolesCount=4 KnotsCount=2 Degree=3 IsPeriodic=0
    g59: BSplineCurve PolesCount=4 KnotsCount=2 Degree=3 IsPeriodic=0
    g60: BSplineCurve PolesCount=4 KnotsCount=2 Degree=3 IsPeriodic=0
    g61: BSplineCurve PolesCount=4 KnotsCount=2 Degree=3 IsPeriodic=0
    g62: BSplineCurve PolesCount=4 KnotsCount=2 Degree=3 IsPeriodic=0
    g63: BSplineCurve PolesCount=4 KnotsCount=2 Degree=3 IsPeriodic=0
    g64: BSplineCurve PolesCount=4 KnotsCount=2 Degree=3 IsPeriodic=0
    g65: BSplineCurve PolesCount=4 KnotsCount=2 Degree=3 IsPeriodic=0
    g66: BSplineCurve PolesCount=4 KnotsCount=2 Degree=3 IsPeriodic=0
    g67: BSplineCurve PolesCount=4 KnotsCount=2 Degree=3 IsPeriodic=0
    g68: BSplineCurve PolesCount=4 KnotsCount=2 Degree=3 IsPeriodic=0
    g69: BSplineCurve PolesCount=4 KnotsCount=2 Degree=3 IsPeriodic=0
    g70: BSplineCurve PolesCount=4 KnotsCount=2 Degree=3 IsPeriodic=0
    g71: BSplineCurve PolesCount=4 KnotsCount=2 Degree=3 IsPeriodic=0
    g72: BSplineCurve PolesCount=4 KnotsCount=2 Degree=3 IsPeriodic=0
    g73: BSplineCurve PolesCount=4 KnotsCount=2 Degree=3 IsPeriodic=0
    g74: BSplineCurve PolesCount=4 KnotsCount=2 Degree=3 IsPeriodic=0
    g75: BSplineCurve PolesCount=4 KnotsCount=2 Degree=3 IsPeriodic=0
    g76: BSplineCurve PolesCount=4 KnotsCount=2 Degree=3 IsPeriodic=0
    g77: BSplineCurve PolesCount=4 KnotsCount=2 Degree=3 IsPeriodic=0
    g78: BSplineCurve PolesCount=4 KnotsCount=2 Degree=3 IsPeriodic=0
    g79: BSplineCurve PolesCount=4 KnotsCount=2 Degree=3 IsPeriodic=0
    g80: BSplineCurve PolesCount=4 KnotsCount=2 Degree=3 IsPeriodic=0
    g81: BSplineCurve PolesCount=4 KnotsCount=2 Degree=3 IsPeriodic=0
    g82: BSplineCurve PolesCount=4 KnotsCount=2 Degree=3 IsPeriodic=0
    g83: BSplineCurve PolesCount=4 KnotsCount=2 Degree=3 IsPeriodic=0
    g84: BSplineCurve PolesCount=4 KnotsCount=2 Degree=3 IsPeriodic=0
    g85: BSplineCurve PolesCount=4 KnotsCount=2 Degree=3 IsPeriodic=0
    g86: BSplineCurve PolesCount=4 KnotsCount=2 Degree=3 IsPeriodic=0
    g87: BSplineCurve PolesCount=4 KnotsCount=2 Degree=3 IsPeriodic=0
    g88: BSplineCurve PolesCount=4 KnotsCount=2 Degree=3 IsPeriodic=0
    g89: BSplineCurve PolesCount=4 KnotsCount=2 Degree=3 IsPeriodic=0
    g90: BSplineCurve PolesCount=4 KnotsCount=2 Degree=3 IsPeriodic=0
    g91: BSplineCurve PolesCount=4 KnotsCount=2 Degree=3 IsPeriodic=0
    g92: BSplineCurve PolesCount=4 KnotsCount=2 Degree=3 IsPeriodic=0
    g93: BSplineCurve PolesCount=4 KnotsCount=2 Degree=3 IsPeriodic=0
    g94: BSplineCurve PolesCount=4 KnotsCount=2 Degree=3 IsPeriodic=0
    g95: BSplineCurve PolesCount=4 KnotsCount=2 Degree=3 IsPeriodic=0
    g96: BSplineCurve PolesCount=4 KnotsCount=2 Degree=3 IsPeriodic=0
    g97: BSplineCurve PolesCount=4 KnotsCount=2 Degree=3 IsPeriodic=0
    g98: BSplineCurve PolesCount=4 KnotsCount=2 Degree=3 IsPeriodic=0
    g99: BSplineCurve PolesCount=4 KnotsCount=2 Degree=3 IsPeriodic=0
    g100: BSplineCurve PolesCount=4 KnotsCount=2 Degree=3 IsPeriodic=0
    g101: BSplineCurve PolesCount=4 KnotsCount=2 Degree=3 IsPeriodic=0
    g102: BSplineCurve PolesCount=4 KnotsCount=2 Degree=3 IsPeriodic=0
    g103: BSplineCurve PolesCount=4 KnotsCount=2 Degree=3 IsPeriodic=0
    g104: BSplineCurve PolesCount=4 KnotsCount=2 Degree=3 IsPeriodic=0
    g105: BSplineCurve PolesCount=4 KnotsCount=2 Degree=3 IsPeriodic=0
    g106: BSplineCurve PolesCount=4 KnotsCount=2 Degree=3 IsPeriodic=0
    g107: BSplineCurve PolesCount=4 KnotsCount=2 Degree=3 IsPeriodic=0
    g108: BSplineCurve PolesCount=4 KnotsCount=2 Degree=3 IsPeriodic=0
    g109: BSplineCurve PolesCount=4 KnotsCount=2 Degree=3 IsPeriodic=0
    g110: BSplineCurve PolesCount=4 KnotsCount=2 Degree=3 IsPeriodic=0
    g111: BSplineCurve PolesCount=4 KnotsCount=2 Degree=3 IsPeriodic=0
    g112: BSplineCurve PolesCount=4 KnotsCount=2 Degree=3 IsPeriodic=0
    g113: BSplineCurve PolesCount=4 KnotsCount=2 Degree=3 IsPeriodic=0
    g114: BSplineCurve PolesCount=4 KnotsCount=2 Degree=3 IsPeriodic=0
    g115: BSplineCurve PolesCount=4 KnotsCount=2 Degree=3 IsPeriodic=0
    g116: BSplineCurve PolesCount=4 KnotsCount=2 Degree=3 IsPeriodic=0
    g117: BSplineCurve PolesCount=4 KnotsCount=2 Degree=3 IsPeriodic=0
    g118: BSplineCurve PolesCount=4 KnotsCount=2 Degree=3 IsPeriodic=0
    g119: BSplineCurve PolesCount=4 KnotsCount=2 Degree=3 IsPeriodic=0
    g120: BSplineCurve PolesCount=4 KnotsCount=2 Degree=3 IsPeriodic=0
    g121: BSplineCurve PolesCount=4 KnotsCount=2 Degree=3 IsPeriodic=0
    g122: BSplineCurve PolesCount=4 KnotsCount=2 Degree=3 IsPeriodic=0
    g123: BSplineCurve PolesCount=4 KnotsCount=2 Degree=3 IsPeriodic=0
    g124: BSplineCurve PolesCount=4 KnotsCount=2 Degree=3 IsPeriodic=0
    g125: BSplineCurve PolesCount=4 KnotsCount=2 Degree=3 IsPeriodic=0
    g126: BSplineCurve PolesCount=4 KnotsCount=2 Degree=3 IsPeriodic=0
    g127: BSplineCurve PolesCount=4 KnotsCount=2 Degree=3 IsPeriodic=0
    g128: BSplineCurve PolesCount=4 KnotsCount=2 Degree=3 IsPeriodic=0
    g129: BSplineCurve PolesCount=4 KnotsCount=2 Degree=3 IsPeriodic=0
    g130: BSplineCurve PolesCount=4 KnotsCount=2 Degree=3 IsPeriodic=0
    g131: BSplineCurve PolesCount=4 KnotsCount=2 Degree=3 IsPeriodic=0
    g132: BSplineCurve PolesCount=4 KnotsCount=2 Degree=3 IsPeriodic=0
    g133: BSplineCurve PolesCount=4 KnotsCount=2 Degree=3 IsPeriodic=0
    g134: BSplineCurve PolesCount=4 KnotsCount=2 Degree=3 IsPeriodic=0
    g135: BSplineCurve PolesCount=4 KnotsCount=2 Degree=3 IsPeriodic=0
    g136: BSplineCurve PolesCount=4 KnotsCount=2 Degree=3 IsPeriodic=0
    g137: BSplineCurve PolesCount=4 KnotsCount=2 Degree=3 IsPeriodic=0
    g138: BSplineCurve PolesCount=4 KnotsCount=2 Degree=3 IsPeriodic=0
    g139: BSplineCurve PolesCount=4 KnotsCount=2 Degree=3 IsPeriodic=0
    g140: BSplineCurve PolesCount=4 KnotsCount=2 Degree=3 IsPeriodic=0
    g141: BSplineCurve PolesCount=4 KnotsCount=2 Degree=3 IsPeriodic=0
    g142: BSplineCurve PolesCount=4 KnotsCount=2 Degree=3 IsPeriodic=0
    g143: BSplineCurve PolesCount=4 KnotsCount=2 Degree=3 IsPeriodic=0
    g144: BSplineCurve PolesCount=4 KnotsCount=2 Degree=3 IsPeriodic=0
    g145: BSplineCurve PolesCount=4 KnotsCount=2 Degree=3 IsPeriodic=0
    g146: BSplineCurve PolesCount=4 KnotsCount=2 Degree=3 IsPeriodic=0
    g147: BSplineCurve PolesCount=4 KnotsCount=2 Degree=3 IsPeriodic=0
    g148: BSplineCurve PolesCount=4 KnotsCount=2 Degree=3 IsPeriodic=0
    g149: BSplineCurve PolesCount=4 KnotsCount=2 Degree=3 IsPeriodic=0
    g150: BSplineCurve PolesCount=4 KnotsCount=2 Degree=3 IsPeriodic=0
    g151: BSplineCurve PolesCount=4 KnotsCount=2 Degree=3 IsPeriodic=0
    g152: BSplineCurve PolesCount=4 KnotsCount=2 Degree=3 IsPeriodic=0
    g153: BSplineCurve PolesCount=4 KnotsCount=2 Degree=3 IsPeriodic=0
    g154: BSplineCurve PolesCount=4 KnotsCount=2 Degree=3 IsPeriodic=0
    g155: BSplineCurve PolesCount=4 KnotsCount=2 Degree=3 IsPeriodic=0
    g156: BSplineCurve PolesCount=4 KnotsCount=2 Degree=3 IsPeriodic=0
    g157: BSplineCurve PolesCount=4 KnotsCount=2 Degree=3 IsPeriodic=0
    g158: BSplineCurve PolesCount=4 KnotsCount=2 Degree=3 IsPeriodic=0
    g159: BSplineCurve PolesCount=4 KnotsCount=2 Degree=3 IsPeriodic=0
    g160: BSplineCurve PolesCount=4 KnotsCount=2 Degree=3 IsPeriodic=0
    g161: BSplineCurve PolesCount=4 KnotsCount=2 Degree=3 IsPeriodic=0
    g162: BSplineCurve PolesCount=4 KnotsCount=2 Degree=3 IsPeriodic=0
    g163: BSplineCurve PolesCount=4 KnotsCount=2 Degree=3 IsPeriodic=0
    g164: BSplineCurve PolesCount=4 KnotsCount=2 Degree=3 IsPeriodic=0
    g165: BSplineCurve PolesCount=4 KnotsCount=2 Degree=3 IsPeriodic=0
    g166: BSplineCurve PolesCount=4 KnotsCount=2 Degree=3 IsPeriodic=0
    g167: BSplineCurve PolesCount=4 KnotsCount=2 Degree=3 IsPeriodic=0
    g168: BSplineCurve PolesCount=4 KnotsCount=2 Degree=3 IsPeriodic=0
    g169: BSplineCurve PolesCount=4 KnotsCount=2 Degree=3 IsPeriodic=0
    g170: BSplineCurve PolesCount=4 KnotsCount=2 Degree=3 IsPeriodic=0
    g171: BSplineCurve PolesCount=4 KnotsCount=2 Degree=3 IsPeriodic=0
    g172: BSplineCurve PolesCount=4 KnotsCount=2 Degree=3 IsPeriodic=0
    g173: BSplineCurve PolesCount=4 KnotsCount=2 Degree=3 IsPeriodic=0
    g174: BSplineCurve PolesCount=4 KnotsCount=2 Degree=3 IsPeriodic=0
    g175: BSplineCurve PolesCount=4 KnotsCount=2 Degree=3 IsPeriodic=0
    g176: BSplineCurve PolesCount=4 KnotsCount=2 Degree=3 IsPeriodic=0
    g177: BSplineCurve PolesCount=4 KnotsCount=2 Degree=3 IsPeriodic=0
    g178: BSplineCurve PolesCount=4 KnotsCount=2 Degree=3 IsPeriodic=0
    g179: BSplineCurve PolesCount=4 KnotsCount=2 Degree=3 IsPeriodic=0
    g180: BSplineCurve PolesCount=4 KnotsCount=2 Degree=3 IsPeriodic=0
    g181: BSplineCurve PolesCount=4 KnotsCount=2 Degree=3 IsPeriodic=0
    g182: BSplineCurve PolesCount=4 KnotsCount=2 Degree=3 IsPeriodic=0
    g183: BSplineCurve PolesCount=4 KnotsCount=2 Degree=3 IsPeriodic=0
    g184: BSplineCurve PolesCount=4 KnotsCount=2 Degree=3 IsPeriodic=0
    g185: BSplineCurve PolesCount=4 KnotsCount=2 Degree=3 IsPeriodic=0
    g186: BSplineCurve PolesCount=4 KnotsCount=2 Degree=3 IsPeriodic=0
    g187: BSplineCurve PolesCount=4 KnotsCount=2 Degree=3 IsPeriodic=0
    g188: BSplineCurve PolesCount=4 KnotsCount=2 Degree=3 IsPeriodic=0
    g189: BSplineCurve PolesCount=4 KnotsCount=2 Degree=3 IsPeriodic=0
    g190: BSplineCurve PolesCount=4 KnotsCount=2 Degree=3 IsPeriodic=0
    g191: BSplineCurve PolesCount=4 KnotsCount=2 Degree=3 IsPeriodic=0
    g192: BSplineCurve PolesCount=4 KnotsCount=2 Degree=3 IsPeriodic=0
    g193: BSplineCurve PolesCount=4 KnotsCount=2 Degree=3 IsPeriodic=0
    g194: BSplineCurve PolesCount=4 KnotsCount=2 Degree=3 IsPeriodic=0
    g195: BSplineCurve PolesCount=4 KnotsCount=2 Degree=3 IsPeriodic=0
    g196: BSplineCurve PolesCount=4 KnotsCount=2 Degree=3 IsPeriodic=0
    g197: BSplineCurve PolesCount=4 KnotsCount=2 Degree=3 IsPeriodic=0
    g198: BSplineCurve PolesCount=4 KnotsCount=2 Degree=3 IsPeriodic=0
    g199: BSplineCurve PolesCount=4 KnotsCount=2 Degree=3 IsPeriodic=0
    g200: BSplineCurve PolesCount=4 KnotsCount=2 Degree=3 IsPeriodic=0
    g201: BSplineCurve PolesCount=4 KnotsCount=2 Degree=3 IsPeriodic=0
    g202: BSplineCurve PolesCount=4 KnotsCount=2 Degree=3 IsPeriodic=0
    g203: BSplineCurve PolesCount=4 KnotsCount=2 Degree=3 IsPeriodic=0
    g204: BSplineCurve PolesCount=4 KnotsCount=2 Degree=3 IsPeriodic=0
    g205: BSplineCurve PolesCount=4 KnotsCount=2 Degree=3 IsPeriodic=0
    g206: BSplineCurve PolesCount=4 KnotsCount=2 Degree=3 IsPeriodic=0
    g207: BSplineCurve PolesCount=4 KnotsCount=2 Degree=3 IsPeriodic=0
    g208: BSplineCurve PolesCount=4 KnotsCount=2 Degree=3 IsPeriodic=0
    g209: BSplineCurve PolesCount=4 KnotsCount=2 Degree=3 IsPeriodic=0
    g210: BSplineCurve PolesCount=4 KnotsCount=2 Degree=3 IsPeriodic=0
    g211: BSplineCurve PolesCount=4 KnotsCount=2 Degree=3 IsPeriodic=0
    g212: BSplineCurve PolesCount=4 KnotsCount=2 Degree=3 IsPeriodic=0
    g213: BSplineCurve PolesCount=4 KnotsCount=2 Degree=3 IsPeriodic=0
    g214: BSplineCurve PolesCount=4 KnotsCount=2 Degree=3 IsPeriodic=0
    g215: BSplineCurve PolesCount=4 KnotsCount=2 Degree=3 IsPeriodic=0
    g216: BSplineCurve PolesCount=4 KnotsCount=2 Degree=3 IsPeriodic=0
    g217: BSplineCurve PolesCount=4 KnotsCount=2 Degree=3 IsPeriodic=0
    g218: BSplineCurve PolesCount=4 KnotsCount=2 Degree=3 IsPeriodic=0
    g219: BSplineCurve PolesCount=4 KnotsCount=2 Degree=3 IsPeriodic=0
    g220: BSplineCurve PolesCount=4 KnotsCount=2 Degree=3 IsPeriodic=0
    g221: BSplineCurve PolesCount=4 KnotsCount=2 Degree=3 IsPeriodic=0
    g222: BSplineCurve PolesCount=4 KnotsCount=2 Degree=3 IsPeriodic=0
    g223: BSplineCurve PolesCount=4 KnotsCount=2 Degree=3 IsPeriodic=0
    g224: BSplineCurve PolesCount=4 KnotsCount=2 Degree=3 IsPeriodic=0
    g225: BSplineCurve PolesCount=4 KnotsCount=2 Degree=3 IsPeriodic=0
    g226: BSplineCurve PolesCount=4 KnotsCount=2 Degree=3 IsPeriodic=0
    g227: BSplineCurve PolesCount=4 KnotsCount=2 Degree=3 IsPeriodic=0
    g228: BSplineCurve PolesCount=4 KnotsCount=2 Degree=3 IsPeriodic=0
    g229: BSplineCurve PolesCount=4 KnotsCount=2 Degree=3 IsPeriodic=0
    g230: BSplineCurve PolesCount=4 KnotsCount=2 Degree=3 IsPeriodic=0
    g231: BSplineCurve PolesCount=4 KnotsCount=2 Degree=3 IsPeriodic=0
    g232: BSplineCurve PolesCount=4 KnotsCount=2 Degree=3 IsPeriodic=0
    g233: BSplineCurve PolesCount=4 KnotsCount=2 Degree=3 IsPeriodic=0
    g234: BSplineCurve PolesCount=4 KnotsCount=2 Degree=3 IsPeriodic=0
    g235: BSplineCurve PolesCount=4 KnotsCount=2 Degree=3 IsPeriodic=0
    g236: BSplineCurve PolesCount=4 KnotsCount=2 Degree=3 IsPeriodic=0
    g237: BSplineCurve PolesCount=4 KnotsCount=2 Degree=3 IsPeriodic=0
    g238: BSplineCurve PolesCount=4 KnotsCount=2 Degree=3 IsPeriodic=0
    g239: BSplineCurve PolesCount=4 KnotsCount=2 Degree=3 IsPeriodic=0
    g240: BSplineCurve PolesCount=4 KnotsCount=2 Degree=3 IsPeriodic=0
    g241: BSplineCurve PolesCount=4 KnotsCount=2 Degree=3 IsPeriodic=0
    g242: BSplineCurve PolesCount=4 KnotsCount=2 Degree=3 IsPeriodic=0
    g243: BSplineCurve PolesCount=4 KnotsCount=2 Degree=3 IsPeriodic=0
    g244: BSplineCurve PolesCount=4 KnotsCount=2 Degree=3 IsPeriodic=0
    g245: BSplineCurve PolesCount=4 KnotsCount=2 Degree=3 IsPeriodic=0
    g246: BSplineCurve PolesCount=4 KnotsCount=2 Degree=3 IsPeriodic=0
    g247: BSplineCurve PolesCount=4 KnotsCount=2 Degree=3 IsPeriodic=0
    g248: BSplineCurve PolesCount=4 KnotsCount=2 Degree=3 IsPeriodic=0
    g249: BSplineCurve PolesCount=4 KnotsCount=2 Degree=3 IsPeriodic=0
    g250: BSplineCurve PolesCount=4 KnotsCount=2 Degree=3 IsPeriodic=0
    g251: BSplineCurve PolesCount=4 KnotsCount=2 Degree=3 IsPeriodic=0
    g252: BSplineCurve PolesCount=4 KnotsCount=2 Degree=3 IsPeriodic=0
    g253: BSplineCurve PolesCount=4 KnotsCount=2 Degree=3 IsPeriodic=0
    g254: BSplineCurve PolesCount=4 KnotsCount=2 Degree=3 IsPeriodic=0
    g255: BSplineCurve PolesCount=4 KnotsCount=2 Degree=3 IsPeriodic=0
    g256: BSplineCurve PolesCount=4 KnotsCount=2 Degree=3 IsPeriodic=0
    g257: BSplineCurve PolesCount=4 KnotsCount=2 Degree=3 IsPeriodic=0
    g258: BSplineCurve PolesCount=4 KnotsCount=2 Degree=3 IsPeriodic=0
    g259: BSplineCurve PolesCount=4 KnotsCount=2 Degree=3 IsPeriodic=0
    g260: BSplineCurve PolesCount=4 KnotsCount=2 Degree=3 IsPeriodic=0
    g261: BSplineCurve PolesCount=4 KnotsCount=2 Degree=3 IsPeriodic=0
    g262: BSplineCurve PolesCount=4 KnotsCount=2 Degree=3 IsPeriodic=0
    g263: BSplineCurve PolesCount=4 KnotsCount=2 Degree=3 IsPeriodic=0
    g264: BSplineCurve PolesCount=4 KnotsCount=2 Degree=3 IsPeriodic=0
    g265: BSplineCurve PolesCount=4 KnotsCount=2 Degree=3 IsPeriodic=0
    g266: BSplineCurve PolesCount=4 KnotsCount=2 Degree=3 IsPeriodic=0
    g267: BSplineCurve PolesCount=4 KnotsCount=2 Degree=3 IsPeriodic=0
    g268: BSplineCurve PolesCount=4 KnotsCount=2 Degree=3 IsPeriodic=0
    g269: BSplineCurve PolesCount=4 KnotsCount=2 Degree=3 IsPeriodic=0
    g270: BSplineCurve PolesCount=4 KnotsCount=2 Degree=3 IsPeriodic=0
    g271: BSplineCurve PolesCount=4 KnotsCount=2 Degree=3 IsPeriodic=0
    g272: BSplineCurve PolesCount=4 KnotsCount=2 Degree=3 IsPeriodic=0
    g273: BSplineCurve PolesCount=4 KnotsCount=2 Degree=3 IsPeriodic=0
    g274: BSplineCurve PolesCount=4 KnotsCount=2 Degree=3 IsPeriodic=0
    g275: BSplineCurve PolesCount=4 KnotsCount=2 Degree=3 IsPeriodic=0
    g276: BSplineCurve PolesCount=4 KnotsCount=2 Degree=3 IsPeriodic=0
    g277: BSplineCurve PolesCount=4 KnotsCount=2 Degree=3 IsPeriodic=0
    g278: LineSegment StartX=-22.7835 StartY=52.5803 StartZ=0 EndX=-24.7911 EndY=49.0325 EndZ=0
    g279: LineSegment StartX=-24.7628 StartY=52.0337 StartZ=0 EndX=-26.2775 EndY=49.1697 EndZ=0
    g280: ArcOfCircle CenterX=-26.9498 CenterY=49.5253 CenterZ=0 NormalX=0 NormalY=0 NormalZ=1 AngleXU=0 Radius=0.760523 StartAngle=4.84877 EndAngle=5.7967
    g281: ArcOfCircle CenterX=-25.03 CenterY=52.1751 CenterZ=0 NormalX=0 NormalY=0 NormalZ=1 AngleXU=0 Radius=0.302288 StartAngle=5.7967 EndAngle=8.02385
  constraints (281):
    c: Coincident(g0,g1)
    c: Coincident(g1,g2)
    c: Coincident(g2,g3)
    c: Coincident(g3,g4)
    c: Coincident(g4,g5)
    c: Coincident(g5,g6)
    c: Coincident(g6,g7)
    c: Coincident(g7,g8)
    c: Coincident(g8,g9)
    c: Coincident(g9,g10)
    c: Coincident(g10,g11)
    c: Coincident(g11,g12)
    c: Coincident(g12,g13)
    c: Coincident(g13,g14)
    c: Coincident(g14,g15)
    c: Coincident(g15,g16)
    c: Coincident(g16,g17)
    c: Coincident(g17,g18)
    c: Coincident(g18,g19)
    c: Coincident(g19,g20)
    c: Coincident(g20,g21)
    c: Coincident(g21,g22)
    c: Coincident(g22,g23)
    c: Coincident(g23,g24)
    c: Coincident(g24,g25)
    c: Coincident(g25,g26)
    c: Coincident(g26,g27)
    c: Coincident(g27,g28)
    c: Coincident(g28,g29)
    c: Coincident(g29,g30)
    c: Coincident(g30,g31)
    c: Coincident(g31,g32)
    c: Coincident(g32,g33)
    c: Coincident(g33,g34)
    c: Coincident(g34,g35)
    c: Coincident(g35,g36)
    c: Coincident(g36,g37)
    c: Coincident(g37,g38)
    c: Coincident(g38,g39)
    c: Coincident(g39,g40)
    c: Coincident(g40,g41)
    c: Coincident(g41,g42)
    c: Coincident(g42,g43)
    c: Coincident(g43,g44)
    c: Coincident(g44,g45)
    c: Coincident(g45,g46)
    c: Coincident(g46,g47)
    c: Coincident(g47,g48)
    c: Coincident(g48,g49)
    c: Coincident(g49,g50)
    c: Coincident(g50,g51)
    c: Coincident(g51,g52)
    c: Coincident(g52,g53)
    c: Coincident(g53,g54)
    c: Coincident(g54,g55)
    c: Coincident(g55,g56)
    c: Coincident(g56,g57)
    c: Coincident(g57,g58)
    c: Coincident(g58,g59)
    c: Coincident(g59,g60)
    c: Coincident(g61,g62)
    c: Coincident(g63,g64)
    c: Coincident(g64,g65)
    c: Coincident(g65,g66)
    c: Coincident(g66,g67)
    c: Coincident(g67,g68)
    c: Coincident(g68,g69)
    c: Coincident(g69,g70)
    c: Coincident(g70,g71)
    c: Coincident(g71,g72)
    c: Coincident(g72,g73)
    c: Coincident(g73,g74)
    c: Coincident(g74,g75)
    c: Coincident(g75,g76)
    c: Coincident(g76,g77)
    c: Coincident(g77,g78)
    c: Coincident(g78,g79)
    c: Coincident(g79,g80)
    c: Coincident(g80,g81)
    c: Coincident(g81,g82)
    c: Coincident(g82,g83)
    c: Coincident(g83,g84)
    c: Coincident(g84,g85)
    c: Coincident(g85,g86)
    c: Coincident(g86,g61)
    c: Coincident(g87,g88)
    c: Coincident(g88,g89)
    c: Coincident(g89,g90)
    c: Coincident(g90,g91)
    c: Coincident(g91,g92)
    c: Coincident(g92,g93)
    c: Coincident(g93,g94)
    c: Coincident(g94,g95)
    c: Coincident(g95,g96)
    c: Coincident(g96,g97)
    c: Coincident(g97,g98)
    c: Coincident(g98,g99)
    c: Coincident(g99,g100)
    c: Coincident(g100,g101)
    c: Coincident(g101,g102)
    c: Coincident(g102,g103)
    c: Coincident(g103,g104)
    c: Coincident(g104,g105)
    c: Coincident(g105,g106)
    c: Coincident(g106,g107)
    c: Coincident(g107,g108)
    c: Coincident(g109,g110)
    c: Coincident(g110,g111)
    c: Coincident(g111,g112)
    c: Coincident(g112,g113)
    c: Coincident(g113,g114)
    c: Coincident(g114,g115)
    c: Coincident(g115,g116)
    c: Coincident(g116,g117)
    c: Coincident(g117,g118)
    c: Coincident(g118,g119)
    c: Coincident(g119,g120)
    c: Coincident(g120,g121)
    c: Coincident(g121,g122)
    c: Coincident(g122,g123)
    c: Coincident(g123,g124)
    c: Coincident(g124,g125)
    c: Coincident(g125,g126)
    c: Coincident(g126,g127)
    c: Coincident(g127,g128)
    c: Coincident(g128,g129)
    c: Coincident(g129,g130)
    c: Coincident(g130,g131)
    c: Coincident(g131,g132)
    c: Coincident(g132,g133)
    c: Coincident(g133,g134)
    c: Coincident(g134,g135)
    c: Coincident(g135,g136)
    c: Coincident(g136,g137)
    c: Coincident(g137,g138)
    c: Coincident(g138,g139)
    c: Coincident(g139,g140)
    c: Coincident(g140,g141)
    c: Coincident(g141,g142)
    c: Coincident(g142,g143)
    c: Coincident(g143,g144)
    c: Coincident(g144,g145)
    c: Coincident(g145,g146)
    c: Coincident(g146,g147)
    c: Coincident(g147,g148)
    c: Coincident(g148,g149)
    c: Coincident(g149,g150)
    c: Coincident(g150,g151)
    c: Coincident(g151,g152)
    c: Coincident(g152,g109)
    c: Coincident(g153,g154)
    c: Coincident(g154,g155)
    c: Coincident(g155,g156)
    c: Coincident(g156,g157)
    c: Coincident(g157,g158)
    c: Coincident(g158,g159)
    c: Coincident(g159,g160)
    c: Coincident(g160,g161)
    c: Coincident(g161,g162)
    c: Coincident(g162,g163)
    c: Coincident(g163,g164)
    c: Coincident(g164,g165)
    c: Coincident(g165,g166)
    c: Coincident(g166,g167)
    c: Coincident(g167,g168)
    c: Coincident(g168,g169)
    c: Coincident(g169,g170)
    c: Coincident(g170,g171)
    c: Coincident(g171,g172)
    c: Coincident(g172,g173)
    c: Coincident(g173,g174)
    c: Coincident(g174,g175)
    c: Coincident(g175,g176)
    c: Coincident(g176,g177)
    c: Coincident(g177,g178)
    c: Coincident(g178,g179)
    c: Coincident(g179,g180)
    c: Coincident(g180,g181)
    c: Coincident(g181,g182)
    c: Coincident(g182,g183)
    c: Coincident(g183,g184)
    c: Coincident(g184,g185)
    c: Coincident(g185,g186)
    c: Coincident(g186,g187)
    c: Coincident(g187,g188)
    c: Coincident(g188,g189)
    c: Coincident(g189,g190)
    c: Coincident(g190,g191)
    c: Coincident(g191,g192)
    c: Coincident(g192,g193)
    c: Coincident(g193,g194)
    c: Coincident(g194,g195)
    c: Coincident(g195,g196)
    c: Coincident(g196,g197)
    c: Coincident(g197,g198)
    c: Coincident(g198,g199)
    c: Coincident(g199,g200)
    c: Coincident(g200,g201)
    c: Coincident(g201,g202)
    c: Coincident(g202,g203)
    c: Coincident(g203,g204)
    c: Coincident(g204,g205)
    c: Coincident(g205,g206)
    c: Coincident(g206,g207)
    c: Coincident(g207,g208)
    c: Coincident(g208,g209)
    c: Coincident(g209,g153)
    c: Coincident(g210,g211)
    c: Coincident(g211,g212)
    c: Coincident(g212,g213)
    c: Coincident(g213,g214)
    c: Coincident(g214,g215)
    c: Coincident(g215,g216)
    c: Coincident(g216,g217)
    c: Coincident(g217,g218)
    c: Coincident(g218,g219)
    c: Coincident(g219,g220)
    c: Coincident(g220,g221)
    c: Coincident(g221,g222)
    c: Coincident(g222,g223)
    c: Coincident(g223,g224)
    c: Coincident(g224,g225)
    c: Coincident(g225,g226)
    c: Coincident(g226,g227)
    c: Coincident(g227,g228)
    c: Coincident(g228,g229)
    c: Coincident(g229,g230)
    c: Coincident(g230,g231)
    c: Coincident(g231,g232)
    c: Coincident(g232,g233)
    c: Coincident(g233,g234)
    c: Coincident(g234,g235)
    c: Coincident(g235,g236)
    c: Coincident(g236,g237)
    c: Coincident(g237,g238)
    c: Coincident(g238,g239)
    c: Coincident(g239,g240)
    c: Coincident(g240,g241)
    c: Coincident(g241,g242)
    c: Coincident(g242,g243)
    c: Coincident(g243,g244)
    c: Coincident(g244,g245)
    c: Coincident(g245,g246)
    c: Coincident(g246,g247)
    c: Coincident(g247,g248)
    c: Coincident(g248,g210)
    c: Coincident(g249,g250)
    c: Coincident(g250,g251)
    c: Coincident(g251,g252)
    c: Coincident(g252,g253)
    c: Coincident(g253,g254)
    c: Coincident(g254,g255)
    c: Coincident(g255,g256)
    c: Coincident(g256,g257)
    c: Coincident(g257,g258)
    c: Coincident(g258,g259)
    c: Coincident(g259,g260)
    c: Coincident(g260,g261)
    c: Coincident(g261,g262)
    c: Coincident(g263,g264)
    c: Coincident(g264,g265)
    c: Coincident(g265,g266)
    c: Coincident(g266,g267)
    c: Coincident(g267,g268)
    c: Coincident(g268,g269)
    c: Coincident(g269,g270)
    c: Coincident(g270,g271)
    c: Coincident(g271,g272)
    c: Coincident(g272,g273)
    c: Coincident(g273,g274)
    c: Coincident(g275,g276)
    c: Coincident(g276,g277)
    c: Coincident(g60,g249)
    c: Coincident(g87,g262)
    c: Coincident(g263,g108)
    c: Coincident(g278,g63)
    c: Coincident(g278,g275)
    c: Tangent(g279,g280) = 1.5708
    c: Tangent(g277,g280) = -1.5708
    c: Tangent(g279,g281) = 1.5708
    c: Coincident(g62,g281)
FEATURE [Mesh::Feature] Mesh001  label="Cut001 (Meshed)001"
FEATURE [Mesh::Feature] Mesh002  label="Body004 (Meshed)"
FEATURE [Sketcher::SketchObject] Sketch033
  MapMode = 5
  Placement = pos=(0,0,1.2) rot=(0,0,1;0rad)
  sketch-geometry (10):
    g0: LineSegment StartX=-9.1 StartY=19.5 StartZ=0 EndX=9.1 EndY=19.5 EndZ=0
    g1: LineSegment StartX=9.1 StartY=19.5 StartZ=0 EndX=9.1 EndY=-17.1 EndZ=0
    g2: LineSegment StartX=9.1 StartY=-17.1 StartZ=0 EndX=-9.1 EndY=-17.1 EndZ=0
    g3: LineSegment StartX=-9.1 StartY=-17.1 StartZ=0 EndX=-9.1 EndY=19.5 EndZ=0
    g4: LineSegment [constr] StartX=-10 StartY=-18.1 StartZ=0 EndX=-9.1 EndY=-17.1 EndZ=0
    g5: LineSegment [constr] StartX=9.1 StartY=-17.1 StartZ=0 EndX=10 EndY=-18.1 EndZ=0
    g6: LineSegment StartX=-9.9 StartY=20.3 StartZ=0 EndX=9.9 EndY=20.3 EndZ=0
    g7: LineSegment StartX=9.9 StartY=20.3 StartZ=0 EndX=9.9 EndY=-17.9 EndZ=0
    g8: LineSegment StartX=9.9 StartY=-17.9 StartZ=0 EndX=-9.9 EndY=-17.9 EndZ=0
    g9: LineSegment StartX=-9.9 StartY=-17.9 StartZ=0 EndX=-9.9 EndY=20.3 EndZ=0
  constraints (25):
    c: Coincident(g0,g1)
    c: Coincident(g1,g2)
    c: Coincident(g2,g3)
    c: Coincident(g3,g0)
    c: Horizontal(g0)
    c: Horizontal(g2)
    c: Vertical(g1)
    c: Vertical(g3)
    c: DistanceX(g0,g0) = 18.2
    c: DistanceY(g1,g1) = 36.6
    c: Coincident(g4,g2)
    c: Coincident(g5,g1)
    c: Equal(g5,g4)
    c: Coincident(g6,g7)
    c: Coincident(g7,g8)
    c: Coincident(g8,g9)
    c: Coincident(g9,g6)
    c: Horizontal(g6)
    c: Horizontal(g8)
    c: Vertical(g7)
    c: Vertical(g9)
    c: DistanceY(g7,g1) = 0.8
    c: DistanceX(g1,g7) = 0.8
    c: DistanceX(g8,g2) = 0.8
    c: DistanceY(g0,g6) = 0.8
FEATURE [Sketcher::SketchObject] Sketch034
  MapMode = 5
  Support = -> [XY_Plane006]
  sketch-geometry (8):
    g0: LineSegment StartX=-10 StartY=24.5 StartZ=0 EndX=10 EndY=24.5 EndZ=0
    g1: ArcOfCircle CenterX=10 CenterY=21.5 CenterZ=0 NormalX=0 NormalY=0 NormalZ=1 AngleXU=0 Radius=3 StartAngle=6e-16 EndAngle=1.5708
    g2: LineSegment StartX=13 StartY=21.5 StartZ=0 EndX=13 EndY=-16.3 EndZ=0
    g3: ArcOfCircle CenterX=10 CenterY=-16.3 CenterZ=0 NormalX=0 NormalY=0 NormalZ=1 AngleXU=0 Radius=3 StartAngle=4.71239 EndAngle=6.28319
    g4: LineSegment StartX=10 StartY=-19.3 StartZ=0 EndX=-10 EndY=-19.3 EndZ=0
    g5: ArcOfCircle CenterX=-10 CenterY=-16.3 CenterZ=0 NormalX=0 NormalY=0 NormalZ=1 AngleXU=0 Radius=3 StartAngle=3.14159 EndAngle=4.71239
    g6: LineSegment StartX=-13 StartY=-16.3 StartZ=0 EndX=-13 EndY=21.5 EndZ=0
    g7: ArcOfCircle CenterX=-10 CenterY=21.5 CenterZ=0 NormalX=0 NormalY=0 NormalZ=1 AngleXU=0 Radius=3 StartAngle=1.5708 EndAngle=3.14159
  constraints (20):
    c: Horizontal(g0)
    c: Tangent(g0,g1) = 1.5708
    c: Tangent(g1,g2) = 1.5708
    c: Tangent(g2,g3) = 1.5708
    c: Tangent(g3,g4) = 1.5708
    c: Tangent(g4,g5) = 1.5708
    c: Tangent(g5,g6) = 1.5708
    c: Tangent(g6,g7) = 1.5708
    c: Equal(g5,g7)
    c: Tangent(g7,g0) = 1.5708
    c: Vertical(g2)
    c: Vertical(g6)
    c: Horizontal(g4)
    c: Equal(g7,g1)
    c: Equal(g1,g3)
    c: Radius(g7) = 3
    c: DistanceX(g0,g0) = 20
    c: DistanceY(g6,g6) = 37.8
    c: DistanceX(g7,g-1) = 10
    c: DistanceY(g3,g-1) = 16.3
FEATURE [PartDesign::Pad] Pad016
  Length = 1
  Length2 = 100
  Profile = -> Sketch034
  Refine = true
  Type = 0
FEATURE [Sketcher::SketchObject] Sketch035
  ExternalGeometry = -> [Pad016]
  MapMode = 5
  Support = -> [XY_Plane006]
  sketch-geometry (16):
    g0: LineSegment StartX=-10 StartY=23.2 StartZ=0 EndX=10 EndY=23.2 EndZ=0
    g1: LineSegment StartX=11.7 StartY=21.5 StartZ=0 EndX=11.7 EndY=-16.3 EndZ=0
    g2: LineSegment StartX=10 StartY=-18 StartZ=0 EndX=-10 EndY=-18 EndZ=0
    g3: LineSegment StartX=-11.7 StartY=-16.3 StartZ=0 EndX=-11.7 EndY=21.5 EndZ=0
    g4: ArcOfCircle CenterX=-10 CenterY=21.5 CenterZ=0 NormalX=0 NormalY=0 NormalZ=1 AngleXU=0 Radius=1.7 StartAngle=1.5708 EndAngle=3.14159
    g5: ArcOfCircle CenterX=10 CenterY=21.5 CenterZ=0 NormalX=0 NormalY=0 NormalZ=1 AngleXU=0 Radius=1.7 StartAngle=-9e-16 EndAngle=1.5708
    g6: ArcOfCircle CenterX=-10 CenterY=-16.3 CenterZ=0 NormalX=0 NormalY=0 NormalZ=1 AngleXU=0 Radius=1.7 StartAngle=3.14159 EndAngle=4.71239
    g7: ArcOfCircle CenterX=10 CenterY=-16.3 CenterZ=0 NormalX=0 NormalY=0 NormalZ=1 AngleXU=0 Radius=1.7 StartAngle=4.71239 EndAngle=6.28319
    g8: LineSegment StartX=-10 StartY=22.4 StartZ=0 EndX=10 EndY=22.4 EndZ=0
    g9: LineSegment StartX=10.9 StartY=21.5 StartZ=0 EndX=10.9 EndY=-16.3 EndZ=0
    g10: LineSegment StartX=10 StartY=-17.2 StartZ=0 EndX=-10 EndY=-17.2 EndZ=0
    g11: LineSegment StartX=-10.9 StartY=-16.3 StartZ=0 EndX=-10.9 EndY=21.5 EndZ=0
    g12: ArcOfCircle CenterX=-10 CenterY=21.5 CenterZ=0 NormalX=0 NormalY=0 NormalZ=1 AngleXU=0 Radius=0.9 StartAngle=1.5708 EndAngle=3.14159
    g13: ArcOfCircle CenterX=10 CenterY=21.5 CenterZ=0 NormalX=0 NormalY=0 NormalZ=1 AngleXU=0 Radius=0.9 StartAngle=-9e-16 EndAngle=1.5708
    g14: ArcOfCircle CenterX=10 CenterY=-16.3 CenterZ=0 NormalX=0 NormalY=0 NormalZ=1 AngleXU=0 Radius=0.9 StartAngle=4.71239 EndAngle=6.28319
    g15: ArcOfCircle CenterX=-10 CenterY=-16.3 CenterZ=0 NormalX=0 NormalY=0 NormalZ=1 AngleXU=0 Radius=0.9 StartAngle=3.14159 EndAngle=4.71239
  constraints (37):
    c: Horizontal(g0)
    c: Horizontal(g2)
    c: Vertical(g1)
    c: Vertical(g3)
    c: Tangent(g3,g4) = 1.5708
    c: Tangent(g0,g4) = 1.5708
    c: Tangent(g0,g5) = 1.5708
    c: Tangent(g1,g5) = 1.5708
    c: Tangent(g3,g6) = 1.5708
    c: Tangent(g2,g6) = 1.5708
    c: Tangent(g2,g7) = 1.5708
    c: Tangent(g1,g7) = 1.5708
    c: Equal(g4,g5)
    c: Equal(g5,g7)
    c: Equal(g7,g6)
    c: DistanceX(g3,g-3) = 1.7
    c: DistanceY(g0,g-3) = 1.3
    c: Vertical(g0,g-3)
    c: DistanceY(g-4,g2) = 1.3
    c: Vertical(g0,g-3)
    c: Horizontal(g8)
    c: Horizontal(g10)
    c: Vertical(g9)
    c: Vertical(g11)
    c: Tangent(g8,g12) = 1.5708
    c: Tangent(g11,g12) = 1.5708
    c: Tangent(g9,g13) = 1.5708
    c: Tangent(g8,g13) = 1.5708
    c: Tangent(g9,g14) = 1.5708
    c: Tangent(g10,g14) = 1.5708
    c: Tangent(g10,g15) = 1.5708
    c: Tangent(g11,g15) = 1.5708
    c: Horizontal(g11,g3)
    c: Coincident(g13,g5)
    c: Coincident(g15,g6)
    c: Coincident(g14,g7)
    c: DistanceX(g3,g11) = 0.8
FEATURE [PartDesign::Pad] Pad017
  BaseFeature = -> Pad016
  Length = 2
  Length2 = 100
  Profile = -> Sketch035
  Refine = true
  Reversed = true
  Type = 0
FEATURE [Sketcher::SketchObject] Sketch036
  ExternalGeometry = -> [Pad017]
  MapMode = 5
  Placement = pos=(11.7,0,0) rot=(0.57735,0.57735,0.57735;2.0944rad)
  Support = -> [Pad017]
  sketch-geometry (6):
    g0: LineSegment StartX=-0.4 StartY=-1.6 StartZ=0 EndX=5.6 EndY=-1.6 EndZ=0
    g1: LineSegment StartX=5.6 StartY=-1.6 StartZ=0 EndX=5.6 EndY=-2 EndZ=0
    g2: LineSegment StartX=5.6 StartY=-2 StartZ=0 EndX=-0.4 EndY=-2 EndZ=0
    g3: LineSegment StartX=-0.4 StartY=-2 StartZ=0 EndX=-0.4 EndY=-1.6 EndZ=0
    g4: LineSegment [constr] StartX=-16.3 StartY=-2 StartZ=0 EndX=-0.4 EndY=-2 EndZ=0
    g5: LineSegment [constr] StartX=5.6 StartY=-2 StartZ=0 EndX=21.5 EndY=-2 EndZ=0
  constraints (16):
    c: Coincident(g0,g1)
    c: Coincident(g1,g2)
    c: Coincident(g2,g3)
    c: Coincident(g3,g0)
    c: Horizontal(g0)
    c: Horizontal(g2)
    c: Vertical(g1)
    c: Vertical(g3)
    c: Coincident(g4,g-3)
    c: Coincident(g4,g2)
    c: Horizontal(g4)
    c: Coincident(g5,g1)
    c: Coincident(g5,g-3)
    c: Equal(g5,g4)
    c: DistanceX(g2,g2) = 6
    c: DistanceY(g1,g1) = 0.4
FEATURE [PartDesign::Pad] Pad018
  BaseFeature = -> Pad017
  Length = 0.4
  Length2 = 100
  Profile = -> Sketch036
  Refine = true
  Type = 0
FEATURE [PartDesign::Mirrored] Mirrored
  BaseFeature = -> Pad018
  MirrorPlane = -> YZ_Plane005
  Originals = -> [Pad018]
  Refine = true
FEATURE [PartDesign::Body] Body005  label="Top"
  Group = -> [Sketch034,Pad016,Sketch035,Pad017,Sketch036,Pad018,Mirrored]
  Origin = -> Origin005
  Placement = pos=(0,0,17) rot=(0,0,1;0rad)
  Tip = -> Mirrored
FEATURE [Sketcher::SketchObject] Sketch037
  ExternalGeometry = -> [Pocket002]
  MapMode = 5
  Placement = pos=(0,-18.1,0) rot=(0,0.707107,0.707107;3.14159rad)
  Support = -> [Pocket002]
  sketch-geometry (4):
    g0: LineSegment StartX=-7.8 StartY=15.6 StartZ=0 EndX=7.8 EndY=15.6 EndZ=0
    g1: LineSegment StartX=7.8 StartY=15.6 StartZ=0 EndX=7.8 EndY=15 EndZ=0
    g2: LineSegment StartX=7.8 StartY=15 StartZ=0 EndX=-7.8 EndY=15 EndZ=0
    g3: LineSegment StartX=-7.8 StartY=15 StartZ=0 EndX=-7.8 EndY=15.6 EndZ=0
  constraints (12):
    c: Coincident(g0,g1)
    c: Coincident(g1,g2)
    c: Coincident(g2,g3)
    c: Coincident(g3,g0)
    c: Horizontal(g0)
    c: Horizontal(g2)
    c: Vertical(g1)
    c: Vertical(g3)
    c: DistanceX(g0,g-3) = -4
    c: DistanceX(g-4,g0) = -4
    c: DistanceY(g3,g3) = 0.6
    c: DistanceY(g0,g-3) = 1.4
FEATURE [PartDesign::Pocket] Pocket003
  BaseFeature = -> Pocket002
  Length = 0.4
  Length2 = 41.8
  Profile = -> Sketch037
  Refine = true
  Type = 4
FEATURE [PartDesign::Pad] Pad015  label="ProMicroHolder"
  BaseFeature = -> Pocket003
  Length = 1
  Length2 = 100
  Profile = -> Sketch033
  Refine = true
  Type = 0
FEATURE [Sketcher::SketchObject] Sketch038
  ExternalGeometry = -> [Pad015]
  MapMode = 5
  Placement = pos=(-11.8,0,0) rot=(0.57735,0.57735,0.57735;2.0944rad)
  Support = -> [Pad015]
  sketch-geometry (4):
    g0: LineSegment StartX=-14.1 StartY=15.6 StartZ=0 EndX=19.3 EndY=15.6 EndZ=0
    g1: LineSegment StartX=19.3 StartY=15.6 StartZ=0 EndX=19.3 EndY=15 EndZ=0
    g2: LineSegment StartX=19.3 StartY=15 StartZ=0 EndX=-14.1 EndY=15 EndZ=0
    g3: LineSegment StartX=-14.1 StartY=15 StartZ=0 EndX=-14.1 EndY=15.6 EndZ=0
  constraints (12):
    c: Coincident(g0,g1)
    c: Coincident(g1,g2)
    c: Coincident(g2,g3)
    c: Coincident(g3,g0)
    c: Horizontal(g0)
    c: Horizontal(g2)
    c: Vertical(g1)
    c: Vertical(g3)
    c: DistanceY(g3,g3) = 0.6
    c: DistanceY(g0,g-3) = 1.4
    c: DistanceX(g-3,g0) = 4
    c: DistanceX(g0,g-3) = 4
FEATURE [PartDesign::Pocket] Pocket004
  BaseFeature = -> Pad015
  Length = 0.4
  Length2 = 24
  Profile = -> Sketch038
  Refine = true
  Type = 4
FEATURE [PartDesign::Fillet] Fillet
  Base = -> Pocket004 [Edge10,Edge5,Edge2,Edge1]
  BaseFeature = -> Pocket004
  Radius = 3
FEATURE [PartDesign::Fillet] Fillet003
  Base = -> Fillet [Edge55,Edge46,Edge39,Edge40]
  BaseFeature = -> Fillet
  Radius = 2
FEATURE [PartDesign::Body] Body
  Group = -> [Sketch,Pad,Sketch004,Pocket,Sketch006,Pocket001,Sketch013,Pocket002,Pocket003,Sketch037,Sketch033,Pad015,Sketch038,Pocket004,Fillet,Fillet003]
  Origin = -> Origin
  Tip = -> Fillet003
FEATURE [Part::Cut] Cut
  Base = -> Body
  Refine = true
  Tool = -> Extrude
FEATURE [Part::Cut] Cut001
  Base = -> Cut
  Refine = true
  Tool = -> Extrude001
note: 2 file-system paths scrubbed to <path> (originals preserved in the JSON sidecar)
